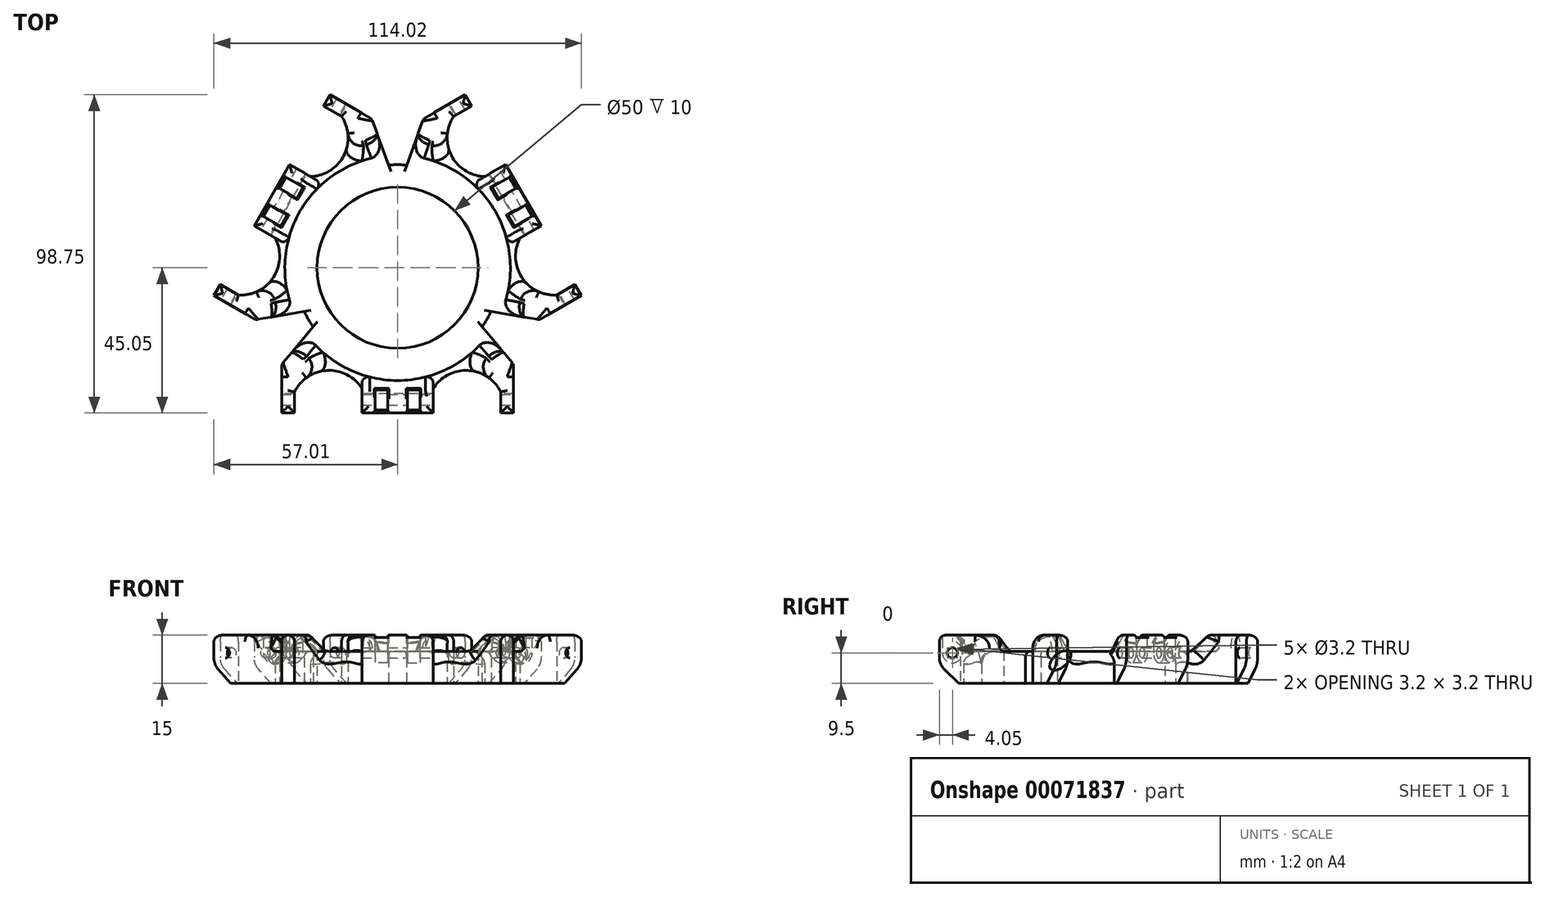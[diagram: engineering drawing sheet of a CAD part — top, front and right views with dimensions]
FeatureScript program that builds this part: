
annotation { "Feature Type Name" : "Feature", "Feature Type Description" : "" }
export const myFeature = defineFeature(function(context is Context, id is Id, definition is map)
    precondition{}
    {
        {
            assignVariable(context, id + "F0", {"name" : "JointHeight", "anyValue" : 18});
        }
        {
            var Q0;
            Q0=qCreatedBy(makeId("Top.planeOp"),FACE);
            var sketch = newSketch(context, id + "F1", { "sketchPlane" : qUnion([Q0])});
            skCircle(sketch, "E0", {"center": v(0, 0) * mm, "radius": 25 * mm});
            skCircle(sketch, "E1", {"center": v(0, 0) * mm, "radius": 32 * mm});
            skSolve(sketch);
        }
        {
            var Q0;
            Q0=qCreatedBy(makeId("Top.planeOp"),FACE);
            var sketch = newSketch(context, id + "F2", { "sketchPlane" : qUnion([Q0])});
            skLineSegment(sketch, "E2", {"start": v(-21.5, 50) * mm, "end": v(-21.5, -50) * mm, "construction": true});
            skLineSegment(sketch, "E3", {"start": v(21.5, 50) * mm, "end": v(21.5, -50) * mm, "construction": true});
            skLineSegment(sketch, "E4", {"start": v(-11, -50) * mm, "end": v(-11, -30.05) * mm, "construction": true});
            skLineSegment(sketch, "E5", {"start": v(11, -50) * mm, "end": v(11, -30.05) * mm, "construction": true});
            skLineSegment(sketch, "E6", {"start": v(-32, -50) * mm, "end": v(-32, 0) * mm, "construction": true});
            skLineSegment(sketch, "E7", {"start": v(32, -50) * mm, "end": v(32, 0) * mm, "construction": true});
            skLineSegment(sketch, "E8", {"start": v(0, -41.5) * mm, "end": v(0, -32) * mm, "construction": true});
            skLineSegment(sketch, "E9", {"start": v(-11, -30.05) * mm, "end": v(-11, -45.05) * mm});
            skLineSegment(sketch, "E10", {"start": v(-11, -45.05) * mm, "end": v(11, -45.05) * mm});
            skLineSegment(sketch, "E11", {"start": v(11, -45.05) * mm, "end": v(11, -30.05) * mm});
            skLineSegment(sketch, "E12", {"start": v(-32, -45.05) * mm, "end": v(-36, -45.05) * mm});
            skArc(sketch, "E13", {"start": v(-11, -30.05) * mm, "mid": v(0, -32) * mm, "end": v(11, -30.05) * mm});
            skLineSegment(sketch, "E14", {"start": v(-36, -45.05) * mm, "end": v(-36, -30.05) * mm});
            skLineSegment(sketch, "E15", {"start": v(-36, -30.05) * mm, "end": v(-26.2, -18.37) * mm});
            skCircle(sketch, "E16", {"center": v(-21.5, -41.5) * mm, "radius": 9.25 * mm, "construction": true});
            skLineSegment(sketch, "E17", {"start": v(-32, -45.05) * mm, "end": v(-32, -38.55) * mm});
            skArc(sketch, "E18", {"start": v(-11, -37.55) * mm, "mid": v(-21.8, -31.88) * mm, "end": v(-32, -38.55) * mm});
            skArc(sketch, "E19", {"start": v(-26.2, -18.37) * mm, "mid": v(-19.5, -25.38) * mm, "end": v(-11, -30.05) * mm});
            skLineSegment(sketch, "E20.MirrorCS", {"start": v(36, -45.05) * mm, "end": v(36, -30.05) * mm});
            skLineSegment(sketch, "E21.MirrorCS", {"start": v(32, -45.05) * mm, "end": v(36, -45.05) * mm});
            skLineSegment(sketch, "E22.MirrorCS", {"start": v(36, -30.05) * mm, "end": v(26.2, -18.37) * mm});
            skLineSegment(sketch, "E23.MirrorCS", {"start": v(32, -45.05) * mm, "end": v(32, -38.55) * mm});
            skArc(sketch, "E24.MirrorCS", {"start": v(11, -37.55) * mm, "mid": v(21.8, -31.88) * mm, "end": v(32, -38.55) * mm});
            skArc(sketch, "E25.MirrorCS", {"start": v(26.2, -18.37) * mm, "mid": v(19.5, -25.38) * mm, "end": v(11, -30.05) * mm});
            skSolve(sketch);
        }
        {
            var Q0;
            Q0=makeQuery(id+"F1.imprint","IMPRINT",FACE,{"disambiguationData":[TD([[makeQuery(id+"F1.imprint","IMPRINT",EDGE,{"derivedFrom":sQuery(id+"F1.wireOp",EDGE,"E0")}),-1.0]])]});
            extrude(context, id + "F3", {"entities" : qUnion([Q0]), "depth" : 10 * mm});
        }
        {
            var Q0;
            Q0=qSketchRegion(id+"F2",true);
            extrude(context, id + "F4", {"entities" : qUnion([Q0]), "depth" : (getVariable(context, 'JointHeight') - 3) * mm});
        }
        {
            var Q0;
            Q0=makeQuery(id+"F4.opExtrude","SWEPT_FACE",FACE,{"disambiguationData":[OSD([sQuery(id+"F2.wireOp",EDGE,"E20.MirrorCS")])]});
            var sketch = newSketch(context, id + "F5", { "sketchPlane" : qUnion([Q0])});
            skCircle(sketch, "E26", {"center": v(-41, 9.5) * mm, "radius": 1.6 * mm});
            skSolve(sketch);
        }
        {
            var Q0;
            Q0=makeQuery(id+"F5.imprint","IMPRINT",FACE,{"disambiguationData":[TD([[makeQuery(id+"F5.imprint","IMPRINT",EDGE,{"derivedFrom":sQuery(id+"F5.wireOp",EDGE,"E26")}),1.0]])]});
            var Q1;
            Q1=makeQuery(id+"F4.opExtrude","SWEPT_FACE",FACE,{"disambiguationData":[OSD([sQuery(id+"F2.wireOp",EDGE,"E14")])]});
            extrude(context, id + "F6", {"entities" : qUnion([Q0]), "operationType" : NewBodyOperationType.REMOVE, "endBound" : BoundingType.UP_TO_SURFACE, "oppositeDirection" : true, "endBoundEntityFace" : qUnion([Q1]), "depth" : 25 * mm});
        }
        {
            var Q0;
            Q0=makeQuery(id+"F4.opExtrude","SWEPT_BODY",BODY,{"disambiguationData":[OSD([sQuery(id+"F2.wireOp",EDGE,"E9"),sQuery(id+"F2.wireOp",EDGE,"E10"),sQuery(id+"F2.wireOp",EDGE,"E11"),sQuery(id+"F2.wireOp",EDGE,"E12"),sQuery(id+"F2.wireOp",EDGE,"E13"),sQuery(id+"F2.wireOp",EDGE,"E14"),sQuery(id+"F2.wireOp",EDGE,"E15"),sQuery(id+"F2.wireOp",EDGE,"E17"),sQuery(id+"F2.wireOp",EDGE,"E18"),sQuery(id+"F2.wireOp",EDGE,"E19"),sQuery(id+"F2.wireOp",EDGE,"E20.MirrorCS"),sQuery(id+"F2.wireOp",EDGE,"E21.MirrorCS"),sQuery(id+"F2.wireOp",EDGE,"E22.MirrorCS"),sQuery(id+"F2.wireOp",EDGE,"E23.MirrorCS"),sQuery(id+"F2.wireOp",EDGE,"E24.MirrorCS"),sQuery(id+"F2.wireOp",EDGE,"E25.MirrorCS")])]});
            var Q1;
            Q1=makeQuery(id+"F3.opExtrude","SWEPT_FACE",FACE,{"disambiguationData":[OSD([sQuery(id+"F1.wireOp",EDGE,"E1")])]});
            circularPattern(context, id + "F7", {"operationType" : NewBodyOperationType.ADD, "entities" : qUnion([Q0]), "axis" : qUnion([Q1]), "angle" : 120 * degree, "instanceCount" : round(3)});
        }
        {
            var Q0;
            Q0=makeQuery(id+"F4.opExtrude","CAP_EDGE",EDGE,{"disambiguationData":[OSD([sQuery(id+"F2.wireOp",EDGE,"E13"),sQuery(id+"F2.wireOp",EDGE,"E19"),sQuery(id+"F2.wireOp",EDGE,"E25.MirrorCS")])],"isStart":false});
            var Q1;
            Q1=makeQuery(id+"F7.opPattern","COPY",EDGE,{"derivedFrom":makeQuery(id+"F4.opExtrude","CAP_EDGE",EDGE,{"disambiguationData":[OSD([sQuery(id+"F2.wireOp",EDGE,"E13"),sQuery(id+"F2.wireOp",EDGE,"E19"),sQuery(id+"F2.wireOp",EDGE,"E25.MirrorCS")])],"isStart":false}),"instanceName":"1"});
            var Q2;
            Q2=makeQuery(id+"F7.opPattern","COPY",EDGE,{"derivedFrom":makeQuery(id+"F4.opExtrude","CAP_EDGE",EDGE,{"disambiguationData":[OSD([sQuery(id+"F2.wireOp",EDGE,"E13"),sQuery(id+"F2.wireOp",EDGE,"E19"),sQuery(id+"F2.wireOp",EDGE,"E25.MirrorCS")])],"isStart":false}),"instanceName":"2"});
            chamfer(context, id + "F8", {"entities" : qUnion([Q0, Q1, Q2]), "width" : 8 * mm});
        }
        {
            var Q0;
            Q0=makeQuery(id+"F8.opChamfer","BLEND_EDGE",EDGE,{"blendedFrom":[makeQuery(id+"F4.opExtrude","CAP_EDGE",EDGE,{"disambiguationData":[OSD([sQuery(id+"F2.wireOp",EDGE,"E13"),sQuery(id+"F2.wireOp",EDGE,"E19"),sQuery(id+"F2.wireOp",EDGE,"E25.MirrorCS")])],"isStart":false}),makeQuery(id+"F4.opExtrude","SWEPT_FACE",FACE,{"disambiguationData":[OSD([sQuery(id+"F2.wireOp",EDGE,"E24.MirrorCS")])]})],"blendedInto":[makeQuery(id+"F4.opExtrude","SWEPT_FACE",FACE,{"disambiguationData":[OSD([sQuery(id+"F2.wireOp",EDGE,"E24.MirrorCS")])]})]});
            var Q1;
            Q1=makeQuery(id+"F8.opChamfer","BLEND_EDGE",EDGE,{"blendedFrom":[makeQuery(id+"F4.opExtrude","CAP_EDGE",EDGE,{"disambiguationData":[OSD([sQuery(id+"F2.wireOp",EDGE,"E13"),sQuery(id+"F2.wireOp",EDGE,"E19"),sQuery(id+"F2.wireOp",EDGE,"E25.MirrorCS")])],"isStart":false}),makeQuery(id+"F4.opExtrude","SWEPT_FACE",FACE,{"disambiguationData":[OSD([sQuery(id+"F2.wireOp",EDGE,"E18")])]})],"blendedInto":[makeQuery(id+"F4.opExtrude","SWEPT_FACE",FACE,{"disambiguationData":[OSD([sQuery(id+"F2.wireOp",EDGE,"E18")])]})]});
            var Q2;
            Q2=makeQuery(id+"F8.opChamfer","BLEND_EDGE",EDGE,{"blendedFrom":[makeQuery(id+"F4.opExtrude","CAP_EDGE",EDGE,{"disambiguationData":[OSD([sQuery(id+"F2.wireOp",EDGE,"E13"),sQuery(id+"F2.wireOp",EDGE,"E19"),sQuery(id+"F2.wireOp",EDGE,"E25.MirrorCS")])],"isStart":false}),makeQuery(id+"F4.opExtrude","SWEPT_FACE",FACE,{"disambiguationData":[OSD([sQuery(id+"F2.wireOp",EDGE,"E22.MirrorCS")])]})],"blendedInto":[makeQuery(id+"F4.opExtrude","SWEPT_FACE",FACE,{"disambiguationData":[OSD([sQuery(id+"F2.wireOp",EDGE,"E22.MirrorCS")])]})]});
            var Q3;
            Q3=makeQuery(id+"F8.opChamfer","BLEND_EDGE",EDGE,{"blendedFrom":[makeQuery(id+"F4.opExtrude","CAP_EDGE",EDGE,{"disambiguationData":[OSD([sQuery(id+"F2.wireOp",EDGE,"E13"),sQuery(id+"F2.wireOp",EDGE,"E19"),sQuery(id+"F2.wireOp",EDGE,"E25.MirrorCS")])],"isStart":false}),makeQuery(id+"F4.opExtrude","SWEPT_FACE",FACE,{"disambiguationData":[OSD([sQuery(id+"F2.wireOp",EDGE,"E15")])]})],"blendedInto":[makeQuery(id+"F4.opExtrude","SWEPT_FACE",FACE,{"disambiguationData":[OSD([sQuery(id+"F2.wireOp",EDGE,"E15")])]})]});
            var Q4;
            Q4=makeQuery(id+"F8.opChamfer","BLEND_EDGE",EDGE,{"blendedFrom":[makeQuery(id+"F7.opPattern","COPY",EDGE,{"derivedFrom":makeQuery(id+"F4.opExtrude","CAP_EDGE",EDGE,{"disambiguationData":[OSD([sQuery(id+"F2.wireOp",EDGE,"E13"),sQuery(id+"F2.wireOp",EDGE,"E19"),sQuery(id+"F2.wireOp",EDGE,"E25.MirrorCS")])],"isStart":false}),"instanceName":"2"}),makeQuery(id+"F7.opPattern","COPY",FACE,{"derivedFrom":makeQuery(id+"F4.opExtrude","SWEPT_FACE",FACE,{"disambiguationData":[OSD([sQuery(id+"F2.wireOp",EDGE,"E18")])]}),"instanceName":"2"})],"blendedInto":[makeQuery(id+"F7.opPattern","COPY",FACE,{"derivedFrom":makeQuery(id+"F4.opExtrude","SWEPT_FACE",FACE,{"disambiguationData":[OSD([sQuery(id+"F2.wireOp",EDGE,"E18")])]}),"instanceName":"2"})]});
            var Q5;
            Q5=makeQuery(id+"F8.opChamfer","BLEND_EDGE",EDGE,{"blendedFrom":[makeQuery(id+"F7.opPattern","COPY",EDGE,{"derivedFrom":makeQuery(id+"F4.opExtrude","CAP_EDGE",EDGE,{"disambiguationData":[OSD([sQuery(id+"F2.wireOp",EDGE,"E13"),sQuery(id+"F2.wireOp",EDGE,"E19"),sQuery(id+"F2.wireOp",EDGE,"E25.MirrorCS")])],"isStart":false}),"instanceName":"1"}),makeQuery(id+"F7.opPattern","COPY",FACE,{"derivedFrom":makeQuery(id+"F4.opExtrude","SWEPT_FACE",FACE,{"disambiguationData":[OSD([sQuery(id+"F2.wireOp",EDGE,"E24.MirrorCS")])]}),"instanceName":"1"})],"blendedInto":[makeQuery(id+"F7.opPattern","COPY",FACE,{"derivedFrom":makeQuery(id+"F4.opExtrude","SWEPT_FACE",FACE,{"disambiguationData":[OSD([sQuery(id+"F2.wireOp",EDGE,"E24.MirrorCS")])]}),"instanceName":"1"})]});
            var Q6;
            Q6=makeQuery(id+"F8.opChamfer","BLEND_EDGE",EDGE,{"blendedFrom":[makeQuery(id+"F7.opPattern","COPY",EDGE,{"derivedFrom":makeQuery(id+"F4.opExtrude","CAP_EDGE",EDGE,{"disambiguationData":[OSD([sQuery(id+"F2.wireOp",EDGE,"E13"),sQuery(id+"F2.wireOp",EDGE,"E19"),sQuery(id+"F2.wireOp",EDGE,"E25.MirrorCS")])],"isStart":false}),"instanceName":"1"}),makeQuery(id+"F7.opPattern","COPY",FACE,{"derivedFrom":makeQuery(id+"F4.opExtrude","SWEPT_FACE",FACE,{"disambiguationData":[OSD([sQuery(id+"F2.wireOp",EDGE,"E18")])]}),"instanceName":"1"})],"blendedInto":[makeQuery(id+"F7.opPattern","COPY",FACE,{"derivedFrom":makeQuery(id+"F4.opExtrude","SWEPT_FACE",FACE,{"disambiguationData":[OSD([sQuery(id+"F2.wireOp",EDGE,"E18")])]}),"instanceName":"1"})]});
            var Q7;
            Q7=makeQuery(id+"F8.opChamfer","BLEND_EDGE",EDGE,{"blendedFrom":[makeQuery(id+"F7.opPattern","COPY",EDGE,{"derivedFrom":makeQuery(id+"F4.opExtrude","CAP_EDGE",EDGE,{"disambiguationData":[OSD([sQuery(id+"F2.wireOp",EDGE,"E13"),sQuery(id+"F2.wireOp",EDGE,"E19"),sQuery(id+"F2.wireOp",EDGE,"E25.MirrorCS")])],"isStart":false}),"instanceName":"2"}),makeQuery(id+"F7.opPattern","COPY",FACE,{"derivedFrom":makeQuery(id+"F4.opExtrude","SWEPT_FACE",FACE,{"disambiguationData":[OSD([sQuery(id+"F2.wireOp",EDGE,"E24.MirrorCS")])]}),"instanceName":"2"})],"blendedInto":[makeQuery(id+"F7.opPattern","COPY",FACE,{"derivedFrom":makeQuery(id+"F4.opExtrude","SWEPT_FACE",FACE,{"disambiguationData":[OSD([sQuery(id+"F2.wireOp",EDGE,"E24.MirrorCS")])]}),"instanceName":"2"})]});
            var Q8;
            Q8=makeQuery(id+"F8.opChamfer","BLEND_EDGE",EDGE,{"blendedFrom":[makeQuery(id+"F7.opPattern","COPY",EDGE,{"derivedFrom":makeQuery(id+"F4.opExtrude","CAP_EDGE",EDGE,{"disambiguationData":[OSD([sQuery(id+"F2.wireOp",EDGE,"E13"),sQuery(id+"F2.wireOp",EDGE,"E19"),sQuery(id+"F2.wireOp",EDGE,"E25.MirrorCS")])],"isStart":false}),"instanceName":"1"}),makeQuery(id+"F7.opPattern","COPY",FACE,{"derivedFrom":makeQuery(id+"F4.opExtrude","SWEPT_FACE",FACE,{"disambiguationData":[OSD([sQuery(id+"F2.wireOp",EDGE,"E22.MirrorCS")])]}),"instanceName":"1"})],"blendedInto":[makeQuery(id+"F7.opPattern","COPY",FACE,{"derivedFrom":makeQuery(id+"F4.opExtrude","SWEPT_FACE",FACE,{"disambiguationData":[OSD([sQuery(id+"F2.wireOp",EDGE,"E22.MirrorCS")])]}),"instanceName":"1"})]});
            var Q9;
            Q9=makeQuery(id+"F8.opChamfer","BLEND_EDGE",EDGE,{"blendedFrom":[makeQuery(id+"F7.opPattern","COPY",EDGE,{"derivedFrom":makeQuery(id+"F4.opExtrude","CAP_EDGE",EDGE,{"disambiguationData":[OSD([sQuery(id+"F2.wireOp",EDGE,"E13"),sQuery(id+"F2.wireOp",EDGE,"E19"),sQuery(id+"F2.wireOp",EDGE,"E25.MirrorCS")])],"isStart":false}),"instanceName":"1"}),makeQuery(id+"F7.opPattern","COPY",FACE,{"derivedFrom":makeQuery(id+"F4.opExtrude","SWEPT_FACE",FACE,{"disambiguationData":[OSD([sQuery(id+"F2.wireOp",EDGE,"E15")])]}),"instanceName":"1"})],"blendedInto":[makeQuery(id+"F7.opPattern","COPY",FACE,{"derivedFrom":makeQuery(id+"F4.opExtrude","SWEPT_FACE",FACE,{"disambiguationData":[OSD([sQuery(id+"F2.wireOp",EDGE,"E15")])]}),"instanceName":"1"})]});
            var Q10;
            Q10=makeQuery(id+"F8.opChamfer","BLEND_EDGE",EDGE,{"blendedFrom":[makeQuery(id+"F7.opPattern","COPY",EDGE,{"derivedFrom":makeQuery(id+"F4.opExtrude","CAP_EDGE",EDGE,{"disambiguationData":[OSD([sQuery(id+"F2.wireOp",EDGE,"E13"),sQuery(id+"F2.wireOp",EDGE,"E19"),sQuery(id+"F2.wireOp",EDGE,"E25.MirrorCS")])],"isStart":false}),"instanceName":"2"}),makeQuery(id+"F7.opPattern","COPY",FACE,{"derivedFrom":makeQuery(id+"F4.opExtrude","SWEPT_FACE",FACE,{"disambiguationData":[OSD([sQuery(id+"F2.wireOp",EDGE,"E22.MirrorCS")])]}),"instanceName":"2"})],"blendedInto":[makeQuery(id+"F7.opPattern","COPY",FACE,{"derivedFrom":makeQuery(id+"F4.opExtrude","SWEPT_FACE",FACE,{"disambiguationData":[OSD([sQuery(id+"F2.wireOp",EDGE,"E22.MirrorCS")])]}),"instanceName":"2"})]});
            var Q11;
            Q11=makeQuery(id+"F7.opPattern","COPY",EDGE,{"derivedFrom":makeQuery(id+"F4.opExtrude","CAP_EDGE",EDGE,{"disambiguationData":[OSD([sQuery(id+"F2.wireOp",EDGE,"E15")])],"isStart":false}),"instanceName":"2"});
            var Q12;
            Q12=makeQuery(id+"F4.opExtrude","CAP_EDGE",EDGE,{"disambiguationData":[OSD([sQuery(id+"F2.wireOp",EDGE,"E22.MirrorCS")])],"isStart":false});
            var Q13;
            Q13=makeQuery(id+"F8.opChamfer","BLEND_EDGE",EDGE,{"blendedFrom":[makeQuery(id+"F7.opPattern","COPY",EDGE,{"derivedFrom":makeQuery(id+"F4.opExtrude","CAP_EDGE",EDGE,{"disambiguationData":[OSD([sQuery(id+"F2.wireOp",EDGE,"E13"),sQuery(id+"F2.wireOp",EDGE,"E19"),sQuery(id+"F2.wireOp",EDGE,"E25.MirrorCS")])],"isStart":false}),"instanceName":"2"}),makeQuery(id+"F7.opPattern","COPY",FACE,{"derivedFrom":makeQuery(id+"F4.opExtrude","SWEPT_FACE",FACE,{"disambiguationData":[OSD([sQuery(id+"F2.wireOp",EDGE,"E15")])]}),"instanceName":"2"})],"blendedInto":[makeQuery(id+"F7.opPattern","COPY",FACE,{"derivedFrom":makeQuery(id+"F4.opExtrude","SWEPT_FACE",FACE,{"disambiguationData":[OSD([sQuery(id+"F2.wireOp",EDGE,"E15")])]}),"instanceName":"2"})]});
            var Q14;
            {var subQ0=sQuery(id+"F1.wireOp",EDGE,"E1");Q14=makeQuery(id+"F8.opChamfer","TWEAK_EDGE",EDGE,{"derivedFrom":[makeQuery(id+"F7.boolean.opBoolean","TWEAK_VERTEX",VERTEX,{"derivedFrom":[makeQuery(id+"F3.opExtrude","CAP_FACE",FACE,{"disambiguationData":[OSD([sQuery(id+"F1.wireOp",EDGE,"E0"),subQ0])],"isStart":false}),makeQuery(id+"F3.opExtrude","SWEPT_FACE",FACE,{"disambiguationData":[OSD([subQ0])]}),makeQuery(id+"F7.opPattern","COPY",FACE,{"derivedFrom":makeQuery(id+"F4.opExtrude","SWEPT_FACE",FACE,{"disambiguationData":[OSD([sQuery(id+"F2.wireOp",EDGE,"E13"),sQuery(id+"F2.wireOp",EDGE,"E19"),sQuery(id+"F2.wireOp",EDGE,"E25.MirrorCS")])]}),"instanceName":"2"}),makeQuery(id+"F7.opPattern","COPY",FACE,{"derivedFrom":makeQuery(id+"F4.opExtrude","SWEPT_FACE",FACE,{"disambiguationData":[OSD([sQuery(id+"F2.wireOp",EDGE,"E22.MirrorCS")])]}),"instanceName":"2"})]})]});}
            var Q15;
            {var subQ0=sQuery(id+"F1.wireOp",EDGE,"E1");Q15=makeQuery(id+"F8.opChamfer","TWEAK_EDGE",EDGE,{"derivedFrom":[makeQuery(id+"F7.boolean.opBoolean","TWEAK_VERTEX",VERTEX,{"derivedFrom":[makeQuery(id+"F3.opExtrude","CAP_FACE",FACE,{"disambiguationData":[OSD([sQuery(id+"F1.wireOp",EDGE,"E0"),subQ0])],"isStart":false}),makeQuery(id+"F3.opExtrude","SWEPT_FACE",FACE,{"disambiguationData":[OSD([subQ0])]}),makeQuery(id+"F7.opPattern","COPY",FACE,{"derivedFrom":makeQuery(id+"F4.opExtrude","SWEPT_FACE",FACE,{"disambiguationData":[OSD([sQuery(id+"F2.wireOp",EDGE,"E13"),sQuery(id+"F2.wireOp",EDGE,"E19"),sQuery(id+"F2.wireOp",EDGE,"E25.MirrorCS")])]}),"instanceName":"1"}),makeQuery(id+"F7.opPattern","COPY",FACE,{"derivedFrom":makeQuery(id+"F4.opExtrude","SWEPT_FACE",FACE,{"disambiguationData":[OSD([sQuery(id+"F2.wireOp",EDGE,"E15")])]}),"instanceName":"1"})]})]});}
            var Q16;
            {var subQ0=sQuery(id+"F1.wireOp",EDGE,"E1");Q16=makeQuery(id+"F8.opChamfer","TWEAK_EDGE",EDGE,{"derivedFrom":[makeQuery(id+"F7.boolean.opBoolean","TWEAK_VERTEX",VERTEX,{"derivedFrom":[makeQuery(id+"F3.opExtrude","CAP_FACE",FACE,{"disambiguationData":[OSD([sQuery(id+"F1.wireOp",EDGE,"E0"),subQ0])],"isStart":false}),makeQuery(id+"F3.opExtrude","SWEPT_FACE",FACE,{"disambiguationData":[OSD([subQ0])]}),makeQuery(id+"F7.opPattern","COPY",FACE,{"derivedFrom":makeQuery(id+"F4.opExtrude","SWEPT_FACE",FACE,{"disambiguationData":[OSD([sQuery(id+"F2.wireOp",EDGE,"E13"),sQuery(id+"F2.wireOp",EDGE,"E19"),sQuery(id+"F2.wireOp",EDGE,"E25.MirrorCS")])]}),"instanceName":"1"}),makeQuery(id+"F7.opPattern","COPY",FACE,{"derivedFrom":makeQuery(id+"F4.opExtrude","SWEPT_FACE",FACE,{"disambiguationData":[OSD([sQuery(id+"F2.wireOp",EDGE,"E22.MirrorCS")])]}),"instanceName":"1"})]})]});}
            var Q17;
            {var subQ0=sQuery(id+"F1.wireOp",EDGE,"E1");Q17=makeQuery(id+"F8.opChamfer","TWEAK_EDGE",EDGE,{"derivedFrom":[makeQuery(id+"F7.boolean.opBoolean","TWEAK_VERTEX",VERTEX,{"derivedFrom":[makeQuery(id+"F3.opExtrude","CAP_FACE",FACE,{"disambiguationData":[OSD([sQuery(id+"F1.wireOp",EDGE,"E0"),subQ0])],"isStart":false}),makeQuery(id+"F3.opExtrude","SWEPT_FACE",FACE,{"disambiguationData":[OSD([subQ0])]}),makeQuery(id+"F4.opExtrude","SWEPT_FACE",FACE,{"disambiguationData":[OSD([sQuery(id+"F2.wireOp",EDGE,"E13"),sQuery(id+"F2.wireOp",EDGE,"E19"),sQuery(id+"F2.wireOp",EDGE,"E25.MirrorCS")])]}),makeQuery(id+"F4.opExtrude","SWEPT_FACE",FACE,{"disambiguationData":[OSD([sQuery(id+"F2.wireOp",EDGE,"E15")])]})]})]});}
            var Q18;
            Q18=makeQuery(id+"F4.opExtrude","CAP_EDGE",EDGE,{"disambiguationData":[OSD([sQuery(id+"F2.wireOp",EDGE,"E15")])],"isStart":false});
            var Q19;
            Q19=makeQuery(id+"F7.opPattern","COPY",EDGE,{"derivedFrom":makeQuery(id+"F4.opExtrude","CAP_EDGE",EDGE,{"disambiguationData":[OSD([sQuery(id+"F2.wireOp",EDGE,"E22.MirrorCS")])],"isStart":false}),"instanceName":"1"});
            var Q20;
            Q20=makeQuery(id+"F7.opPattern","COPY",EDGE,{"derivedFrom":makeQuery(id+"F4.opExtrude","CAP_EDGE",EDGE,{"disambiguationData":[OSD([sQuery(id+"F2.wireOp",EDGE,"E22.MirrorCS")])],"isStart":false}),"instanceName":"2"});
            var Q21;
            Q21=makeQuery(id+"F7.opPattern","COPY",EDGE,{"derivedFrom":makeQuery(id+"F4.opExtrude","CAP_EDGE",EDGE,{"disambiguationData":[OSD([sQuery(id+"F2.wireOp",EDGE,"E15")])],"isStart":false}),"instanceName":"1"});
            var Q22;
            {var subQ0=sQuery(id+"F1.wireOp",EDGE,"E1");Q22=makeQuery(id+"F8.opChamfer","TWEAK_EDGE",EDGE,{"derivedFrom":[makeQuery(id+"F7.boolean.opBoolean","TWEAK_VERTEX",VERTEX,{"derivedFrom":[makeQuery(id+"F3.opExtrude","CAP_FACE",FACE,{"disambiguationData":[OSD([sQuery(id+"F1.wireOp",EDGE,"E0"),subQ0])],"isStart":false}),makeQuery(id+"F3.opExtrude","SWEPT_FACE",FACE,{"disambiguationData":[OSD([subQ0])]}),makeQuery(id+"F7.opPattern","COPY",FACE,{"derivedFrom":makeQuery(id+"F4.opExtrude","SWEPT_FACE",FACE,{"disambiguationData":[OSD([sQuery(id+"F2.wireOp",EDGE,"E13"),sQuery(id+"F2.wireOp",EDGE,"E19"),sQuery(id+"F2.wireOp",EDGE,"E25.MirrorCS")])]}),"instanceName":"2"}),makeQuery(id+"F7.opPattern","COPY",FACE,{"derivedFrom":makeQuery(id+"F4.opExtrude","SWEPT_FACE",FACE,{"disambiguationData":[OSD([sQuery(id+"F2.wireOp",EDGE,"E15")])]}),"instanceName":"2"})]})]});}
            var Q23;
            {var subQ0=sQuery(id+"F1.wireOp",EDGE,"E1");Q23=makeQuery(id+"F8.opChamfer","TWEAK_EDGE",EDGE,{"derivedFrom":[makeQuery(id+"F7.boolean.opBoolean","TWEAK_VERTEX",VERTEX,{"derivedFrom":[makeQuery(id+"F3.opExtrude","CAP_FACE",FACE,{"disambiguationData":[OSD([sQuery(id+"F1.wireOp",EDGE,"E0"),subQ0])],"isStart":false}),makeQuery(id+"F3.opExtrude","SWEPT_FACE",FACE,{"disambiguationData":[OSD([subQ0])]}),makeQuery(id+"F4.opExtrude","SWEPT_FACE",FACE,{"disambiguationData":[OSD([sQuery(id+"F2.wireOp",EDGE,"E13"),sQuery(id+"F2.wireOp",EDGE,"E19"),sQuery(id+"F2.wireOp",EDGE,"E25.MirrorCS")])]}),makeQuery(id+"F4.opExtrude","SWEPT_FACE",FACE,{"disambiguationData":[OSD([sQuery(id+"F2.wireOp",EDGE,"E22.MirrorCS")])]})]})]});}
            fillet(context, id + "F9", {"entities" : qUnion([Q0, Q1, Q2, Q3, Q4, Q5, Q6, Q7, Q8, Q9, Q10, Q11, Q12, Q13, Q14, Q15, Q16, Q17, Q18, Q19, Q20, Q21, Q22, Q23]), "radius" : 4 * mm, "tangentPropagation" : true, "allowEdgeOverflow" : false});
        }
        {
            var Q0;
            Q0=makeQuery(id+"F8.opChamfer","BLEND_EDGE",EDGE,{"blendedFrom":[makeQuery(id+"F7.opPattern","COPY",EDGE,{"derivedFrom":makeQuery(id+"F4.opExtrude","CAP_EDGE",EDGE,{"disambiguationData":[OSD([sQuery(id+"F2.wireOp",EDGE,"E13"),sQuery(id+"F2.wireOp",EDGE,"E19"),sQuery(id+"F2.wireOp",EDGE,"E25.MirrorCS")])],"isStart":false}),"instanceName":"1"}),makeQuery(id+"F7.opPattern","COPY",FACE,{"derivedFrom":makeQuery(id+"F4.opExtrude","SWEPT_FACE",FACE,{"disambiguationData":[OSD([sQuery(id+"F2.wireOp",EDGE,"E11")])]}),"instanceName":"1"})],"blendedInto":[makeQuery(id+"F7.opPattern","COPY",FACE,{"derivedFrom":makeQuery(id+"F4.opExtrude","SWEPT_FACE",FACE,{"disambiguationData":[OSD([sQuery(id+"F2.wireOp",EDGE,"E11")])]}),"instanceName":"1"})]});
            var Q1;
            Q1=makeQuery(id+"F8.opChamfer","BLEND_EDGE",EDGE,{"blendedFrom":[makeQuery(id+"F7.opPattern","COPY",EDGE,{"derivedFrom":makeQuery(id+"F4.opExtrude","CAP_EDGE",EDGE,{"disambiguationData":[OSD([sQuery(id+"F2.wireOp",EDGE,"E13"),sQuery(id+"F2.wireOp",EDGE,"E19"),sQuery(id+"F2.wireOp",EDGE,"E25.MirrorCS")])],"isStart":false}),"instanceName":"1"}),makeQuery(id+"F7.opPattern","COPY",FACE,{"derivedFrom":makeQuery(id+"F4.opExtrude","SWEPT_FACE",FACE,{"disambiguationData":[OSD([sQuery(id+"F2.wireOp",EDGE,"E9")])]}),"instanceName":"1"})],"blendedInto":[makeQuery(id+"F7.opPattern","COPY",FACE,{"derivedFrom":makeQuery(id+"F4.opExtrude","SWEPT_FACE",FACE,{"disambiguationData":[OSD([sQuery(id+"F2.wireOp",EDGE,"E9")])]}),"instanceName":"1"})]});
            var Q2;
            Q2=makeQuery(id+"F8.opChamfer","BLEND_EDGE",EDGE,{"blendedFrom":[makeQuery(id+"F7.opPattern","COPY",EDGE,{"derivedFrom":makeQuery(id+"F4.opExtrude","CAP_EDGE",EDGE,{"disambiguationData":[OSD([sQuery(id+"F2.wireOp",EDGE,"E13"),sQuery(id+"F2.wireOp",EDGE,"E19"),sQuery(id+"F2.wireOp",EDGE,"E25.MirrorCS")])],"isStart":false}),"instanceName":"2"}),makeQuery(id+"F7.opPattern","COPY",FACE,{"derivedFrom":makeQuery(id+"F4.opExtrude","SWEPT_FACE",FACE,{"disambiguationData":[OSD([sQuery(id+"F2.wireOp",EDGE,"E11")])]}),"instanceName":"2"})],"blendedInto":[makeQuery(id+"F7.opPattern","COPY",FACE,{"derivedFrom":makeQuery(id+"F4.opExtrude","SWEPT_FACE",FACE,{"disambiguationData":[OSD([sQuery(id+"F2.wireOp",EDGE,"E11")])]}),"instanceName":"2"})]});
            var Q3;
            Q3=makeQuery(id+"F8.opChamfer","BLEND_EDGE",EDGE,{"blendedFrom":[makeQuery(id+"F7.opPattern","COPY",EDGE,{"derivedFrom":makeQuery(id+"F4.opExtrude","CAP_EDGE",EDGE,{"disambiguationData":[OSD([sQuery(id+"F2.wireOp",EDGE,"E13"),sQuery(id+"F2.wireOp",EDGE,"E19"),sQuery(id+"F2.wireOp",EDGE,"E25.MirrorCS")])],"isStart":false}),"instanceName":"2"}),makeQuery(id+"F7.opPattern","COPY",FACE,{"derivedFrom":makeQuery(id+"F4.opExtrude","SWEPT_FACE",FACE,{"disambiguationData":[OSD([sQuery(id+"F2.wireOp",EDGE,"E9")])]}),"instanceName":"2"})],"blendedInto":[makeQuery(id+"F7.opPattern","COPY",FACE,{"derivedFrom":makeQuery(id+"F4.opExtrude","SWEPT_FACE",FACE,{"disambiguationData":[OSD([sQuery(id+"F2.wireOp",EDGE,"E9")])]}),"instanceName":"2"})]});
            var Q4;
            Q4=makeQuery(id+"F8.opChamfer","BLEND_EDGE",EDGE,{"blendedFrom":[makeQuery(id+"F4.opExtrude","CAP_EDGE",EDGE,{"disambiguationData":[OSD([sQuery(id+"F2.wireOp",EDGE,"E13"),sQuery(id+"F2.wireOp",EDGE,"E19"),sQuery(id+"F2.wireOp",EDGE,"E25.MirrorCS")])],"isStart":false}),makeQuery(id+"F4.opExtrude","SWEPT_FACE",FACE,{"disambiguationData":[OSD([sQuery(id+"F2.wireOp",EDGE,"E11")])]})],"blendedInto":[makeQuery(id+"F4.opExtrude","SWEPT_FACE",FACE,{"disambiguationData":[OSD([sQuery(id+"F2.wireOp",EDGE,"E11")])]})]});
            var Q5;
            Q5=makeQuery(id+"F8.opChamfer","BLEND_EDGE",EDGE,{"blendedFrom":[makeQuery(id+"F4.opExtrude","CAP_EDGE",EDGE,{"disambiguationData":[OSD([sQuery(id+"F2.wireOp",EDGE,"E13"),sQuery(id+"F2.wireOp",EDGE,"E19"),sQuery(id+"F2.wireOp",EDGE,"E25.MirrorCS")])],"isStart":false}),makeQuery(id+"F4.opExtrude","SWEPT_FACE",FACE,{"disambiguationData":[OSD([sQuery(id+"F2.wireOp",EDGE,"E9")])]})],"blendedInto":[makeQuery(id+"F4.opExtrude","SWEPT_FACE",FACE,{"disambiguationData":[OSD([sQuery(id+"F2.wireOp",EDGE,"E9")])]})]});
            var Q6;
            Q6=makeQuery(id+"F8.opChamfer","SPLIT",FACE,{"disambiguationData":[OD(0.0)],"derivedFrom":makeQuery(id+"F4.opExtrude","CAP_FACE",FACE,{"disambiguationData":[OSD([sQuery(id+"F2.wireOp",EDGE,"E9"),sQuery(id+"F2.wireOp",EDGE,"E10"),sQuery(id+"F2.wireOp",EDGE,"E11"),sQuery(id+"F2.wireOp",EDGE,"E12"),sQuery(id+"F2.wireOp",EDGE,"E13"),sQuery(id+"F2.wireOp",EDGE,"E14"),sQuery(id+"F2.wireOp",EDGE,"E15"),sQuery(id+"F2.wireOp",EDGE,"E17"),sQuery(id+"F2.wireOp",EDGE,"E18"),sQuery(id+"F2.wireOp",EDGE,"E19"),sQuery(id+"F2.wireOp",EDGE,"E20.MirrorCS"),sQuery(id+"F2.wireOp",EDGE,"E21.MirrorCS"),sQuery(id+"F2.wireOp",EDGE,"E22.MirrorCS"),sQuery(id+"F2.wireOp",EDGE,"E23.MirrorCS"),sQuery(id+"F2.wireOp",EDGE,"E24.MirrorCS"),sQuery(id+"F2.wireOp",EDGE,"E25.MirrorCS")])],"isStart":false})});
            var Q7;
            Q7=makeQuery(id+"F8.opChamfer","SPLIT",FACE,{"disambiguationData":[OD(1.0)],"derivedFrom":makeQuery(id+"F4.opExtrude","CAP_FACE",FACE,{"disambiguationData":[OSD([sQuery(id+"F2.wireOp",EDGE,"E9"),sQuery(id+"F2.wireOp",EDGE,"E10"),sQuery(id+"F2.wireOp",EDGE,"E11"),sQuery(id+"F2.wireOp",EDGE,"E12"),sQuery(id+"F2.wireOp",EDGE,"E13"),sQuery(id+"F2.wireOp",EDGE,"E14"),sQuery(id+"F2.wireOp",EDGE,"E15"),sQuery(id+"F2.wireOp",EDGE,"E17"),sQuery(id+"F2.wireOp",EDGE,"E18"),sQuery(id+"F2.wireOp",EDGE,"E19"),sQuery(id+"F2.wireOp",EDGE,"E20.MirrorCS"),sQuery(id+"F2.wireOp",EDGE,"E21.MirrorCS"),sQuery(id+"F2.wireOp",EDGE,"E22.MirrorCS"),sQuery(id+"F2.wireOp",EDGE,"E23.MirrorCS"),sQuery(id+"F2.wireOp",EDGE,"E24.MirrorCS"),sQuery(id+"F2.wireOp",EDGE,"E25.MirrorCS")])],"isStart":false})});
            var Q8;
            Q8=makeQuery(id+"F8.opChamfer","SPLIT",FACE,{"disambiguationData":[OD(2.0)],"derivedFrom":makeQuery(id+"F7.opPattern","COPY",FACE,{"derivedFrom":makeQuery(id+"F4.opExtrude","CAP_FACE",FACE,{"disambiguationData":[OSD([sQuery(id+"F2.wireOp",EDGE,"E9"),sQuery(id+"F2.wireOp",EDGE,"E10"),sQuery(id+"F2.wireOp",EDGE,"E11"),sQuery(id+"F2.wireOp",EDGE,"E12"),sQuery(id+"F2.wireOp",EDGE,"E13"),sQuery(id+"F2.wireOp",EDGE,"E14"),sQuery(id+"F2.wireOp",EDGE,"E15"),sQuery(id+"F2.wireOp",EDGE,"E17"),sQuery(id+"F2.wireOp",EDGE,"E18"),sQuery(id+"F2.wireOp",EDGE,"E19"),sQuery(id+"F2.wireOp",EDGE,"E20.MirrorCS"),sQuery(id+"F2.wireOp",EDGE,"E21.MirrorCS"),sQuery(id+"F2.wireOp",EDGE,"E22.MirrorCS"),sQuery(id+"F2.wireOp",EDGE,"E23.MirrorCS"),sQuery(id+"F2.wireOp",EDGE,"E24.MirrorCS"),sQuery(id+"F2.wireOp",EDGE,"E25.MirrorCS")])],"isStart":false}),"instanceName":"1"})});
            var Q9;
            Q9=makeQuery(id+"F8.opChamfer","SPLIT",FACE,{"disambiguationData":[OD(1.0)],"derivedFrom":makeQuery(id+"F7.opPattern","COPY",FACE,{"derivedFrom":makeQuery(id+"F4.opExtrude","CAP_FACE",FACE,{"disambiguationData":[OSD([sQuery(id+"F2.wireOp",EDGE,"E9"),sQuery(id+"F2.wireOp",EDGE,"E10"),sQuery(id+"F2.wireOp",EDGE,"E11"),sQuery(id+"F2.wireOp",EDGE,"E12"),sQuery(id+"F2.wireOp",EDGE,"E13"),sQuery(id+"F2.wireOp",EDGE,"E14"),sQuery(id+"F2.wireOp",EDGE,"E15"),sQuery(id+"F2.wireOp",EDGE,"E17"),sQuery(id+"F2.wireOp",EDGE,"E18"),sQuery(id+"F2.wireOp",EDGE,"E19"),sQuery(id+"F2.wireOp",EDGE,"E20.MirrorCS"),sQuery(id+"F2.wireOp",EDGE,"E21.MirrorCS"),sQuery(id+"F2.wireOp",EDGE,"E22.MirrorCS"),sQuery(id+"F2.wireOp",EDGE,"E23.MirrorCS"),sQuery(id+"F2.wireOp",EDGE,"E24.MirrorCS"),sQuery(id+"F2.wireOp",EDGE,"E25.MirrorCS")])],"isStart":false}),"instanceName":"1"})});
            var Q10;
            Q10=makeQuery(id+"F8.opChamfer","SPLIT",FACE,{"disambiguationData":[OD(0.0)],"derivedFrom":makeQuery(id+"F7.opPattern","COPY",FACE,{"derivedFrom":makeQuery(id+"F4.opExtrude","CAP_FACE",FACE,{"disambiguationData":[OSD([sQuery(id+"F2.wireOp",EDGE,"E9"),sQuery(id+"F2.wireOp",EDGE,"E10"),sQuery(id+"F2.wireOp",EDGE,"E11"),sQuery(id+"F2.wireOp",EDGE,"E12"),sQuery(id+"F2.wireOp",EDGE,"E13"),sQuery(id+"F2.wireOp",EDGE,"E14"),sQuery(id+"F2.wireOp",EDGE,"E15"),sQuery(id+"F2.wireOp",EDGE,"E17"),sQuery(id+"F2.wireOp",EDGE,"E18"),sQuery(id+"F2.wireOp",EDGE,"E19"),sQuery(id+"F2.wireOp",EDGE,"E20.MirrorCS"),sQuery(id+"F2.wireOp",EDGE,"E21.MirrorCS"),sQuery(id+"F2.wireOp",EDGE,"E22.MirrorCS"),sQuery(id+"F2.wireOp",EDGE,"E23.MirrorCS"),sQuery(id+"F2.wireOp",EDGE,"E24.MirrorCS"),sQuery(id+"F2.wireOp",EDGE,"E25.MirrorCS")])],"isStart":false}),"instanceName":"1"})});
            var Q11;
            Q11=makeQuery(id+"F8.opChamfer","SPLIT",FACE,{"disambiguationData":[OD(2.0)],"derivedFrom":makeQuery(id+"F7.opPattern","COPY",FACE,{"derivedFrom":makeQuery(id+"F4.opExtrude","CAP_FACE",FACE,{"disambiguationData":[OSD([sQuery(id+"F2.wireOp",EDGE,"E9"),sQuery(id+"F2.wireOp",EDGE,"E10"),sQuery(id+"F2.wireOp",EDGE,"E11"),sQuery(id+"F2.wireOp",EDGE,"E12"),sQuery(id+"F2.wireOp",EDGE,"E13"),sQuery(id+"F2.wireOp",EDGE,"E14"),sQuery(id+"F2.wireOp",EDGE,"E15"),sQuery(id+"F2.wireOp",EDGE,"E17"),sQuery(id+"F2.wireOp",EDGE,"E18"),sQuery(id+"F2.wireOp",EDGE,"E19"),sQuery(id+"F2.wireOp",EDGE,"E20.MirrorCS"),sQuery(id+"F2.wireOp",EDGE,"E21.MirrorCS"),sQuery(id+"F2.wireOp",EDGE,"E22.MirrorCS"),sQuery(id+"F2.wireOp",EDGE,"E23.MirrorCS"),sQuery(id+"F2.wireOp",EDGE,"E24.MirrorCS"),sQuery(id+"F2.wireOp",EDGE,"E25.MirrorCS")])],"isStart":false}),"instanceName":"2"})});
            var Q12;
            Q12=makeQuery(id+"F8.opChamfer","SPLIT",FACE,{"disambiguationData":[OD(0.0)],"derivedFrom":makeQuery(id+"F7.opPattern","COPY",FACE,{"derivedFrom":makeQuery(id+"F4.opExtrude","CAP_FACE",FACE,{"disambiguationData":[OSD([sQuery(id+"F2.wireOp",EDGE,"E9"),sQuery(id+"F2.wireOp",EDGE,"E10"),sQuery(id+"F2.wireOp",EDGE,"E11"),sQuery(id+"F2.wireOp",EDGE,"E12"),sQuery(id+"F2.wireOp",EDGE,"E13"),sQuery(id+"F2.wireOp",EDGE,"E14"),sQuery(id+"F2.wireOp",EDGE,"E15"),sQuery(id+"F2.wireOp",EDGE,"E17"),sQuery(id+"F2.wireOp",EDGE,"E18"),sQuery(id+"F2.wireOp",EDGE,"E19"),sQuery(id+"F2.wireOp",EDGE,"E20.MirrorCS"),sQuery(id+"F2.wireOp",EDGE,"E21.MirrorCS"),sQuery(id+"F2.wireOp",EDGE,"E22.MirrorCS"),sQuery(id+"F2.wireOp",EDGE,"E23.MirrorCS"),sQuery(id+"F2.wireOp",EDGE,"E24.MirrorCS"),sQuery(id+"F2.wireOp",EDGE,"E25.MirrorCS")])],"isStart":false}),"instanceName":"2"})});
            var Q13;
            Q13=makeQuery(id+"F8.opChamfer","SPLIT",FACE,{"disambiguationData":[OD(1.0)],"derivedFrom":makeQuery(id+"F7.opPattern","COPY",FACE,{"derivedFrom":makeQuery(id+"F4.opExtrude","CAP_FACE",FACE,{"disambiguationData":[OSD([sQuery(id+"F2.wireOp",EDGE,"E9"),sQuery(id+"F2.wireOp",EDGE,"E10"),sQuery(id+"F2.wireOp",EDGE,"E11"),sQuery(id+"F2.wireOp",EDGE,"E12"),sQuery(id+"F2.wireOp",EDGE,"E13"),sQuery(id+"F2.wireOp",EDGE,"E14"),sQuery(id+"F2.wireOp",EDGE,"E15"),sQuery(id+"F2.wireOp",EDGE,"E17"),sQuery(id+"F2.wireOp",EDGE,"E18"),sQuery(id+"F2.wireOp",EDGE,"E19"),sQuery(id+"F2.wireOp",EDGE,"E20.MirrorCS"),sQuery(id+"F2.wireOp",EDGE,"E21.MirrorCS"),sQuery(id+"F2.wireOp",EDGE,"E22.MirrorCS"),sQuery(id+"F2.wireOp",EDGE,"E23.MirrorCS"),sQuery(id+"F2.wireOp",EDGE,"E24.MirrorCS"),sQuery(id+"F2.wireOp",EDGE,"E25.MirrorCS")])],"isStart":false}),"instanceName":"2"})});
            var Q14;
            Q14=makeQuery(id+"F8.opChamfer","SPLIT",FACE,{"disambiguationData":[OD(2.0)],"derivedFrom":makeQuery(id+"F4.opExtrude","CAP_FACE",FACE,{"disambiguationData":[OSD([sQuery(id+"F2.wireOp",EDGE,"E9"),sQuery(id+"F2.wireOp",EDGE,"E10"),sQuery(id+"F2.wireOp",EDGE,"E11"),sQuery(id+"F2.wireOp",EDGE,"E12"),sQuery(id+"F2.wireOp",EDGE,"E13"),sQuery(id+"F2.wireOp",EDGE,"E14"),sQuery(id+"F2.wireOp",EDGE,"E15"),sQuery(id+"F2.wireOp",EDGE,"E17"),sQuery(id+"F2.wireOp",EDGE,"E18"),sQuery(id+"F2.wireOp",EDGE,"E19"),sQuery(id+"F2.wireOp",EDGE,"E20.MirrorCS"),sQuery(id+"F2.wireOp",EDGE,"E21.MirrorCS"),sQuery(id+"F2.wireOp",EDGE,"E22.MirrorCS"),sQuery(id+"F2.wireOp",EDGE,"E23.MirrorCS"),sQuery(id+"F2.wireOp",EDGE,"E24.MirrorCS"),sQuery(id+"F2.wireOp",EDGE,"E25.MirrorCS")])],"isStart":false})});
            fillet(context, id + "F10", {"entities" : qUnion([Q0, Q1, Q2, Q3, Q4, Q5, Q6, Q7, Q8, Q9, Q10, Q11, Q12, Q13, Q14]), "radius" : 2 * mm, "tangentPropagation" : true, "allowEdgeOverflow" : false});
        }
        {
            var Q0;
            {var subQ0=sQuery(id+"F1.wireOp",EDGE,"E1");Q0=makeQuery(id+"F8.opChamfer","TWEAK_EDGE",EDGE,{"derivedFrom":[makeQuery(id+"F7.boolean.opBoolean","TWEAK_VERTEX",VERTEX,{"derivedFrom":[makeQuery(id+"F3.opExtrude","CAP_FACE",FACE,{"disambiguationData":[OSD([sQuery(id+"F1.wireOp",EDGE,"E0"),subQ0])],"isStart":false}),makeQuery(id+"F3.opExtrude","SWEPT_FACE",FACE,{"disambiguationData":[OSD([subQ0])]}),makeQuery(id+"F4.opExtrude","SWEPT_FACE",FACE,{"disambiguationData":[OSD([sQuery(id+"F2.wireOp",EDGE,"E13"),sQuery(id+"F2.wireOp",EDGE,"E19"),sQuery(id+"F2.wireOp",EDGE,"E25.MirrorCS")])]}),makeQuery(id+"F4.opExtrude","SWEPT_FACE",FACE,{"disambiguationData":[OSD([sQuery(id+"F2.wireOp",EDGE,"E15")])]})]})]});}
            var Q1;
            {var subQ0=makeQuery(id+"F4.opExtrude","SWEPT_FACE",FACE,{"disambiguationData":[OSD([sQuery(id+"F2.wireOp",EDGE,"E13"),sQuery(id+"F2.wireOp",EDGE,"E19"),sQuery(id+"F2.wireOp",EDGE,"E25.MirrorCS")])]});var subQ1=sQuery(id+"F1.wireOp",EDGE,"E1");Q1=makeQuery(id+"F7.boolean.opBoolean","SPLIT",EDGE,{"disambiguationData":[TD([makeQuery(id+"F3.opExtrude","CAP_FACE",FACE,{"disambiguationData":[OSD([sQuery(id+"F1.wireOp",EDGE,"E0"),subQ1])],"isStart":false}),makeQuery(id+"F3.opExtrude","SWEPT_FACE",FACE,{"disambiguationData":[OSD([subQ1])]}),subQ0,makeQuery(id+"F4.opExtrude","SWEPT_FACE",FACE,{"disambiguationData":[OSD([sQuery(id+"F2.wireOp",EDGE,"E15")])]}),makeQuery(id+"F7.opPattern","COPY",FACE,{"derivedFrom":subQ0,"instanceName":"1"}),makeQuery(id+"F7.opPattern","COPY",FACE,{"derivedFrom":makeQuery(id+"F4.opExtrude","SWEPT_FACE",FACE,{"disambiguationData":[OSD([sQuery(id+"F2.wireOp",EDGE,"E22.MirrorCS")])]}),"instanceName":"1"})])],"derivedFrom":makeQuery(id+"F3.opExtrude","CAP_EDGE",EDGE,{"disambiguationData":[OSD([subQ1])],"isStart":false})});}
            var Q2;
            {var subQ0=sQuery(id+"F1.wireOp",EDGE,"E1");Q2=makeQuery(id+"F8.opChamfer","TWEAK_EDGE",EDGE,{"derivedFrom":[makeQuery(id+"F7.boolean.opBoolean","TWEAK_VERTEX",VERTEX,{"derivedFrom":[makeQuery(id+"F3.opExtrude","CAP_FACE",FACE,{"disambiguationData":[OSD([sQuery(id+"F1.wireOp",EDGE,"E0"),subQ0])],"isStart":false}),makeQuery(id+"F3.opExtrude","SWEPT_FACE",FACE,{"disambiguationData":[OSD([subQ0])]}),makeQuery(id+"F7.opPattern","COPY",FACE,{"derivedFrom":makeQuery(id+"F4.opExtrude","SWEPT_FACE",FACE,{"disambiguationData":[OSD([sQuery(id+"F2.wireOp",EDGE,"E13"),sQuery(id+"F2.wireOp",EDGE,"E19"),sQuery(id+"F2.wireOp",EDGE,"E25.MirrorCS")])]}),"instanceName":"1"}),makeQuery(id+"F7.opPattern","COPY",FACE,{"derivedFrom":makeQuery(id+"F4.opExtrude","SWEPT_FACE",FACE,{"disambiguationData":[OSD([sQuery(id+"F2.wireOp",EDGE,"E22.MirrorCS")])]}),"instanceName":"1"})]})]});}
            var Q3;
            {var subQ0=sQuery(id+"F1.wireOp",EDGE,"E1");var subQ1=sQuery(id+"F1.wireOp",EDGE,"E0");var subQ3=sQuery(id+"F2.wireOp",EDGE,"E19");var subQ5=sQuery(id+"F2.wireOp",EDGE,"E15");Q3=makeQuery(id+"F7.boolean.opBoolean","SPLIT",EDGE,{"disambiguationData":[TD([makeQuery(id+"F3.opExtrude","CAP_FACE",FACE,{"disambiguationData":[OSD([subQ1,subQ0])],"isStart":true})])],"derivedFrom":makeQuery(id+"F4.opExtrude","SWEPT_EDGE",EDGE,{"disambiguationData":[OSD([subQ5,subQ3])]})});}
            var Q4;
            {var subQ0=sQuery(id+"F1.wireOp",EDGE,"E1");var subQ1=sQuery(id+"F1.wireOp",EDGE,"E0");var subQ2=sQuery(id+"F2.wireOp",EDGE,"E25.MirrorCS");var subQ3=sQuery(id+"F2.wireOp",EDGE,"E22.MirrorCS");Q4=makeQuery(id+"F7.boolean.opBoolean","SPLIT",EDGE,{"disambiguationData":[TD([makeQuery(id+"F3.opExtrude","CAP_FACE",FACE,{"disambiguationData":[OSD([subQ1,subQ0])],"isStart":true})])],"derivedFrom":makeQuery(id+"F7.opPattern","COPY",EDGE,{"derivedFrom":makeQuery(id+"F4.opExtrude","SWEPT_EDGE",EDGE,{"disambiguationData":[OSD([subQ3,subQ2])]}),"instanceName":"1"})});}
            var Q5;
            {var subQ0=sQuery(id+"F1.wireOp",EDGE,"E1");Q5=makeQuery(id+"F8.opChamfer","TWEAK_EDGE",EDGE,{"derivedFrom":[makeQuery(id+"F7.boolean.opBoolean","TWEAK_VERTEX",VERTEX,{"derivedFrom":[makeQuery(id+"F3.opExtrude","CAP_FACE",FACE,{"disambiguationData":[OSD([sQuery(id+"F1.wireOp",EDGE,"E0"),subQ0])],"isStart":false}),makeQuery(id+"F3.opExtrude","SWEPT_FACE",FACE,{"disambiguationData":[OSD([subQ0])]}),makeQuery(id+"F7.opPattern","COPY",FACE,{"derivedFrom":makeQuery(id+"F4.opExtrude","SWEPT_FACE",FACE,{"disambiguationData":[OSD([sQuery(id+"F2.wireOp",EDGE,"E13"),sQuery(id+"F2.wireOp",EDGE,"E19"),sQuery(id+"F2.wireOp",EDGE,"E25.MirrorCS")])]}),"instanceName":"1"}),makeQuery(id+"F7.opPattern","COPY",FACE,{"derivedFrom":makeQuery(id+"F4.opExtrude","SWEPT_FACE",FACE,{"disambiguationData":[OSD([sQuery(id+"F2.wireOp",EDGE,"E15")])]}),"instanceName":"1"})]})]});}
            var Q6;
            {var subQ0=makeQuery(id+"F4.opExtrude","SWEPT_FACE",FACE,{"disambiguationData":[OSD([sQuery(id+"F2.wireOp",EDGE,"E13"),sQuery(id+"F2.wireOp",EDGE,"E19"),sQuery(id+"F2.wireOp",EDGE,"E25.MirrorCS")])]});var subQ1=sQuery(id+"F1.wireOp",EDGE,"E1");Q6=makeQuery(id+"F7.boolean.opBoolean","SPLIT",EDGE,{"disambiguationData":[TD([makeQuery(id+"F3.opExtrude","CAP_FACE",FACE,{"disambiguationData":[OSD([sQuery(id+"F1.wireOp",EDGE,"E0"),subQ1])],"isStart":false}),makeQuery(id+"F3.opExtrude","SWEPT_FACE",FACE,{"disambiguationData":[OSD([subQ1])]}),makeQuery(id+"F7.opPattern","COPY",FACE,{"derivedFrom":subQ0,"instanceName":"1"}),makeQuery(id+"F7.opPattern","COPY",FACE,{"derivedFrom":makeQuery(id+"F4.opExtrude","SWEPT_FACE",FACE,{"disambiguationData":[OSD([sQuery(id+"F2.wireOp",EDGE,"E15")])]}),"instanceName":"1"}),makeQuery(id+"F7.opPattern","COPY",FACE,{"derivedFrom":subQ0,"instanceName":"2"}),makeQuery(id+"F7.opPattern","COPY",FACE,{"derivedFrom":makeQuery(id+"F4.opExtrude","SWEPT_FACE",FACE,{"disambiguationData":[OSD([sQuery(id+"F2.wireOp",EDGE,"E22.MirrorCS")])]}),"instanceName":"2"})])],"derivedFrom":makeQuery(id+"F3.opExtrude","CAP_EDGE",EDGE,{"disambiguationData":[OSD([subQ1])],"isStart":false})});}
            var Q7;
            {var subQ0=sQuery(id+"F1.wireOp",EDGE,"E1");Q7=makeQuery(id+"F8.opChamfer","TWEAK_EDGE",EDGE,{"derivedFrom":[makeQuery(id+"F7.boolean.opBoolean","TWEAK_VERTEX",VERTEX,{"derivedFrom":[makeQuery(id+"F3.opExtrude","CAP_FACE",FACE,{"disambiguationData":[OSD([sQuery(id+"F1.wireOp",EDGE,"E0"),subQ0])],"isStart":false}),makeQuery(id+"F3.opExtrude","SWEPT_FACE",FACE,{"disambiguationData":[OSD([subQ0])]}),makeQuery(id+"F7.opPattern","COPY",FACE,{"derivedFrom":makeQuery(id+"F4.opExtrude","SWEPT_FACE",FACE,{"disambiguationData":[OSD([sQuery(id+"F2.wireOp",EDGE,"E13"),sQuery(id+"F2.wireOp",EDGE,"E19"),sQuery(id+"F2.wireOp",EDGE,"E25.MirrorCS")])]}),"instanceName":"2"}),makeQuery(id+"F7.opPattern","COPY",FACE,{"derivedFrom":makeQuery(id+"F4.opExtrude","SWEPT_FACE",FACE,{"disambiguationData":[OSD([sQuery(id+"F2.wireOp",EDGE,"E22.MirrorCS")])]}),"instanceName":"2"})]})]});}
            var Q8;
            {var subQ0=sQuery(id+"F1.wireOp",EDGE,"E1");var subQ1=sQuery(id+"F1.wireOp",EDGE,"E0");var subQ2=sQuery(id+"F2.wireOp",EDGE,"E25.MirrorCS");var subQ3=sQuery(id+"F2.wireOp",EDGE,"E22.MirrorCS");Q8=makeQuery(id+"F7.boolean.opBoolean","SPLIT",EDGE,{"disambiguationData":[TD([makeQuery(id+"F3.opExtrude","CAP_FACE",FACE,{"disambiguationData":[OSD([subQ1,subQ0])],"isStart":true})])],"derivedFrom":makeQuery(id+"F7.opPattern","COPY",EDGE,{"derivedFrom":makeQuery(id+"F4.opExtrude","SWEPT_EDGE",EDGE,{"disambiguationData":[OSD([subQ3,subQ2])]}),"instanceName":"2"})});}
            var Q9;
            {var subQ0=sQuery(id+"F1.wireOp",EDGE,"E1");var subQ1=sQuery(id+"F1.wireOp",EDGE,"E0");var subQ3=sQuery(id+"F2.wireOp",EDGE,"E19");var subQ4=sQuery(id+"F2.wireOp",EDGE,"E15");Q9=makeQuery(id+"F7.boolean.opBoolean","SPLIT",EDGE,{"disambiguationData":[TD([makeQuery(id+"F3.opExtrude","CAP_FACE",FACE,{"disambiguationData":[OSD([subQ1,subQ0])],"isStart":true})])],"derivedFrom":makeQuery(id+"F7.opPattern","COPY",EDGE,{"derivedFrom":makeQuery(id+"F4.opExtrude","SWEPT_EDGE",EDGE,{"disambiguationData":[OSD([subQ4,subQ3])]}),"instanceName":"1"})});}
            var Q10;
            {var subQ0=sQuery(id+"F1.wireOp",EDGE,"E1");var subQ1=sQuery(id+"F2.wireOp",EDGE,"E22.MirrorCS");var subQ2=sQuery(id+"F1.wireOp",EDGE,"E0");var subQ3=sQuery(id+"F2.wireOp",EDGE,"E25.MirrorCS");Q10=makeQuery(id+"F7.boolean.opBoolean","SPLIT",EDGE,{"disambiguationData":[TD([makeQuery(id+"F3.opExtrude","CAP_FACE",FACE,{"disambiguationData":[OSD([subQ2,subQ0])],"isStart":true})])],"derivedFrom":makeQuery(id+"F4.opExtrude","SWEPT_EDGE",EDGE,{"disambiguationData":[OSD([subQ1,subQ3])]})});}
            var Q11;
            {var subQ0=sQuery(id+"F1.wireOp",EDGE,"E1");var subQ1=sQuery(id+"F1.wireOp",EDGE,"E0");var subQ2=sQuery(id+"F2.wireOp",EDGE,"E15");var subQ4=sQuery(id+"F2.wireOp",EDGE,"E19");Q11=makeQuery(id+"F7.boolean.opBoolean","SPLIT",EDGE,{"disambiguationData":[TD([makeQuery(id+"F3.opExtrude","CAP_FACE",FACE,{"disambiguationData":[OSD([subQ1,subQ0])],"isStart":true})])],"derivedFrom":makeQuery(id+"F7.opPattern","COPY",EDGE,{"derivedFrom":makeQuery(id+"F4.opExtrude","SWEPT_EDGE",EDGE,{"disambiguationData":[OSD([subQ2,subQ4])]}),"instanceName":"2"})});}
            var Q12;
            {var subQ0=sQuery(id+"F1.wireOp",EDGE,"E1");var subQ1=makeQuery(id+"F4.opExtrude","SWEPT_FACE",FACE,{"disambiguationData":[OSD([sQuery(id+"F2.wireOp",EDGE,"E13"),sQuery(id+"F2.wireOp",EDGE,"E19"),sQuery(id+"F2.wireOp",EDGE,"E25.MirrorCS")])]});Q12=makeQuery(id+"F7.boolean.opBoolean","SPLIT",EDGE,{"disambiguationData":[TD([makeQuery(id+"F3.opExtrude","CAP_FACE",FACE,{"disambiguationData":[OSD([sQuery(id+"F1.wireOp",EDGE,"E0"),subQ0])],"isStart":false}),makeQuery(id+"F3.opExtrude","SWEPT_FACE",FACE,{"disambiguationData":[OSD([subQ0])]}),subQ1,makeQuery(id+"F4.opExtrude","SWEPT_FACE",FACE,{"disambiguationData":[OSD([sQuery(id+"F2.wireOp",EDGE,"E22.MirrorCS")])]}),makeQuery(id+"F7.opPattern","COPY",FACE,{"derivedFrom":subQ1,"instanceName":"2"}),makeQuery(id+"F7.opPattern","COPY",FACE,{"derivedFrom":makeQuery(id+"F4.opExtrude","SWEPT_FACE",FACE,{"disambiguationData":[OSD([sQuery(id+"F2.wireOp",EDGE,"E15")])]}),"instanceName":"2"})])],"derivedFrom":makeQuery(id+"F3.opExtrude","CAP_EDGE",EDGE,{"disambiguationData":[OSD([subQ0])],"isStart":false})});}
            var Q13;
            {var subQ0=sQuery(id+"F1.wireOp",EDGE,"E1");Q13=makeQuery(id+"F8.opChamfer","TWEAK_EDGE",EDGE,{"derivedFrom":[makeQuery(id+"F7.boolean.opBoolean","TWEAK_VERTEX",VERTEX,{"derivedFrom":[makeQuery(id+"F3.opExtrude","CAP_FACE",FACE,{"disambiguationData":[OSD([sQuery(id+"F1.wireOp",EDGE,"E0"),subQ0])],"isStart":false}),makeQuery(id+"F3.opExtrude","SWEPT_FACE",FACE,{"disambiguationData":[OSD([subQ0])]}),makeQuery(id+"F4.opExtrude","SWEPT_FACE",FACE,{"disambiguationData":[OSD([sQuery(id+"F2.wireOp",EDGE,"E13"),sQuery(id+"F2.wireOp",EDGE,"E19"),sQuery(id+"F2.wireOp",EDGE,"E25.MirrorCS")])]}),makeQuery(id+"F4.opExtrude","SWEPT_FACE",FACE,{"disambiguationData":[OSD([sQuery(id+"F2.wireOp",EDGE,"E22.MirrorCS")])]})]})]});}
            var Q14;
            {var subQ0=sQuery(id+"F1.wireOp",EDGE,"E1");Q14=makeQuery(id+"F8.opChamfer","TWEAK_EDGE",EDGE,{"derivedFrom":[makeQuery(id+"F7.boolean.opBoolean","TWEAK_VERTEX",VERTEX,{"derivedFrom":[makeQuery(id+"F3.opExtrude","CAP_FACE",FACE,{"disambiguationData":[OSD([sQuery(id+"F1.wireOp",EDGE,"E0"),subQ0])],"isStart":false}),makeQuery(id+"F3.opExtrude","SWEPT_FACE",FACE,{"disambiguationData":[OSD([subQ0])]}),makeQuery(id+"F7.opPattern","COPY",FACE,{"derivedFrom":makeQuery(id+"F4.opExtrude","SWEPT_FACE",FACE,{"disambiguationData":[OSD([sQuery(id+"F2.wireOp",EDGE,"E13"),sQuery(id+"F2.wireOp",EDGE,"E19"),sQuery(id+"F2.wireOp",EDGE,"E25.MirrorCS")])]}),"instanceName":"2"}),makeQuery(id+"F7.opPattern","COPY",FACE,{"derivedFrom":makeQuery(id+"F4.opExtrude","SWEPT_FACE",FACE,{"disambiguationData":[OSD([sQuery(id+"F2.wireOp",EDGE,"E15")])]}),"instanceName":"2"})]})]});}
            fillet(context, id + "F11", {"entities" : qUnion([Q0, Q1, Q2, Q3, Q4, Q5, Q6, Q7, Q8, Q9, Q10, Q11, Q12, Q13, Q14]), "radius" : 2 * mm, "tangentPropagation" : true, "allowEdgeOverflow" : false});
        }
        {
            var Q0;
            Q0=makeQuery(id+"F7.opPattern","COPY",EDGE,{"derivedFrom":makeQuery(id+"F4.opExtrude","CAP_EDGE",EDGE,{"disambiguationData":[OSD([sQuery(id+"F2.wireOp",EDGE,"E21.MirrorCS")])],"isStart":true}),"instanceName":"2"});
            var Q1;
            Q1=makeQuery(id+"F7.opPattern","COPY",EDGE,{"derivedFrom":makeQuery(id+"F4.opExtrude","CAP_EDGE",EDGE,{"disambiguationData":[OSD([sQuery(id+"F2.wireOp",EDGE,"E10")])],"isStart":true}),"instanceName":"2"});
            var Q2;
            Q2=makeQuery(id+"F7.opPattern","COPY",EDGE,{"derivedFrom":makeQuery(id+"F4.opExtrude","CAP_EDGE",EDGE,{"disambiguationData":[OSD([sQuery(id+"F2.wireOp",EDGE,"E12")])],"isStart":true}),"instanceName":"2"});
            var Q3;
            Q3=makeQuery(id+"F7.opPattern","COPY",EDGE,{"derivedFrom":makeQuery(id+"F4.opExtrude","CAP_EDGE",EDGE,{"disambiguationData":[OSD([sQuery(id+"F2.wireOp",EDGE,"E12")])],"isStart":true}),"instanceName":"1"});
            var Q4;
            Q4=makeQuery(id+"F7.opPattern","COPY",EDGE,{"derivedFrom":makeQuery(id+"F4.opExtrude","CAP_EDGE",EDGE,{"disambiguationData":[OSD([sQuery(id+"F2.wireOp",EDGE,"E10")])],"isStart":true}),"instanceName":"1"});
            var Q5;
            Q5=makeQuery(id+"F7.opPattern","COPY",EDGE,{"derivedFrom":makeQuery(id+"F4.opExtrude","CAP_EDGE",EDGE,{"disambiguationData":[OSD([sQuery(id+"F2.wireOp",EDGE,"E21.MirrorCS")])],"isStart":true}),"instanceName":"1"});
            var Q6;
            Q6=makeQuery(id+"F4.opExtrude","CAP_EDGE",EDGE,{"disambiguationData":[OSD([sQuery(id+"F2.wireOp",EDGE,"E12")])],"isStart":true});
            var Q7;
            Q7=makeQuery(id+"F4.opExtrude","CAP_EDGE",EDGE,{"disambiguationData":[OSD([sQuery(id+"F2.wireOp",EDGE,"E10")])],"isStart":true});
            var Q8;
            Q8=makeQuery(id+"F4.opExtrude","CAP_EDGE",EDGE,{"disambiguationData":[OSD([sQuery(id+"F2.wireOp",EDGE,"E21.MirrorCS")])],"isStart":true});
            chamfer(context, id + "F12", {"entities" : qUnion([Q0, Q1, Q2, Q3, Q4, Q5, Q6, Q7, Q8]), "width" : 6 * mm, "tangentPropagation" : true});
        }
        {
            var Q0;
            {var subQ0=sQuery(id+"F2.wireOp",EDGE,"E10");Q0=makeQuery(id+"F12.opChamfer","BLEND_EDGE",EDGE,{"blendedFrom":[makeQuery(id+"F7.opPattern","COPY",EDGE,{"derivedFrom":makeQuery(id+"F4.opExtrude","CAP_EDGE",EDGE,{"disambiguationData":[OSD([subQ0])],"isStart":true}),"instanceName":"1"}),makeQuery(id+"F7.opPattern","COPY",FACE,{"derivedFrom":makeQuery(id+"F4.opExtrude","SWEPT_FACE",FACE,{"disambiguationData":[OSD([subQ0])]}),"instanceName":"1"})],"blendedInto":[makeQuery(id+"F7.opPattern","COPY",FACE,{"derivedFrom":makeQuery(id+"F4.opExtrude","SWEPT_FACE",FACE,{"disambiguationData":[OSD([subQ0])]}),"instanceName":"1"})]});}
            var Q1;
            {var subQ0=sQuery(id+"F2.wireOp",EDGE,"E12");Q1=makeQuery(id+"F12.opChamfer","BLEND_EDGE",EDGE,{"blendedFrom":[makeQuery(id+"F7.opPattern","COPY",EDGE,{"derivedFrom":makeQuery(id+"F4.opExtrude","CAP_EDGE",EDGE,{"disambiguationData":[OSD([subQ0])],"isStart":true}),"instanceName":"1"}),makeQuery(id+"F7.opPattern","COPY",FACE,{"derivedFrom":makeQuery(id+"F4.opExtrude","SWEPT_FACE",FACE,{"disambiguationData":[OSD([subQ0])]}),"instanceName":"1"})],"blendedInto":[makeQuery(id+"F7.opPattern","COPY",FACE,{"derivedFrom":makeQuery(id+"F4.opExtrude","SWEPT_FACE",FACE,{"disambiguationData":[OSD([subQ0])]}),"instanceName":"1"})]});}
            var Q2;
            {var subQ0=sQuery(id+"F2.wireOp",EDGE,"E21.MirrorCS");Q2=makeQuery(id+"F12.opChamfer","BLEND_EDGE",EDGE,{"blendedFrom":[makeQuery(id+"F7.opPattern","COPY",EDGE,{"derivedFrom":makeQuery(id+"F4.opExtrude","CAP_EDGE",EDGE,{"disambiguationData":[OSD([subQ0])],"isStart":true}),"instanceName":"1"}),makeQuery(id+"F7.opPattern","COPY",FACE,{"derivedFrom":makeQuery(id+"F4.opExtrude","SWEPT_FACE",FACE,{"disambiguationData":[OSD([subQ0])]}),"instanceName":"1"})],"blendedInto":[makeQuery(id+"F7.opPattern","COPY",FACE,{"derivedFrom":makeQuery(id+"F4.opExtrude","SWEPT_FACE",FACE,{"disambiguationData":[OSD([subQ0])]}),"instanceName":"1"})]});}
            var Q3;
            {var subQ0=sQuery(id+"F2.wireOp",EDGE,"E12");Q3=makeQuery(id+"F12.opChamfer","BLEND_EDGE",EDGE,{"blendedFrom":[makeQuery(id+"F4.opExtrude","CAP_EDGE",EDGE,{"disambiguationData":[OSD([subQ0])],"isStart":true}),makeQuery(id+"F4.opExtrude","SWEPT_FACE",FACE,{"disambiguationData":[OSD([subQ0])]})],"blendedInto":[makeQuery(id+"F4.opExtrude","SWEPT_FACE",FACE,{"disambiguationData":[OSD([subQ0])]})]});}
            var Q4;
            {var subQ0=sQuery(id+"F2.wireOp",EDGE,"E10");Q4=makeQuery(id+"F12.opChamfer","BLEND_EDGE",EDGE,{"blendedFrom":[makeQuery(id+"F4.opExtrude","CAP_EDGE",EDGE,{"disambiguationData":[OSD([subQ0])],"isStart":true}),makeQuery(id+"F4.opExtrude","SWEPT_FACE",FACE,{"disambiguationData":[OSD([subQ0])]})],"blendedInto":[makeQuery(id+"F4.opExtrude","SWEPT_FACE",FACE,{"disambiguationData":[OSD([subQ0])]})]});}
            var Q5;
            {var subQ0=sQuery(id+"F2.wireOp",EDGE,"E21.MirrorCS");Q5=makeQuery(id+"F12.opChamfer","BLEND_EDGE",EDGE,{"blendedFrom":[makeQuery(id+"F4.opExtrude","CAP_EDGE",EDGE,{"disambiguationData":[OSD([subQ0])],"isStart":true}),makeQuery(id+"F4.opExtrude","SWEPT_FACE",FACE,{"disambiguationData":[OSD([subQ0])]})],"blendedInto":[makeQuery(id+"F4.opExtrude","SWEPT_FACE",FACE,{"disambiguationData":[OSD([subQ0])]})]});}
            var Q6;
            {var subQ0=sQuery(id+"F2.wireOp",EDGE,"E12");Q6=makeQuery(id+"F12.opChamfer","BLEND_EDGE",EDGE,{"blendedFrom":[makeQuery(id+"F7.opPattern","COPY",EDGE,{"derivedFrom":makeQuery(id+"F4.opExtrude","CAP_EDGE",EDGE,{"disambiguationData":[OSD([subQ0])],"isStart":true}),"instanceName":"2"}),makeQuery(id+"F7.opPattern","COPY",FACE,{"derivedFrom":makeQuery(id+"F4.opExtrude","SWEPT_FACE",FACE,{"disambiguationData":[OSD([subQ0])]}),"instanceName":"2"})],"blendedInto":[makeQuery(id+"F7.opPattern","COPY",FACE,{"derivedFrom":makeQuery(id+"F4.opExtrude","SWEPT_FACE",FACE,{"disambiguationData":[OSD([subQ0])]}),"instanceName":"2"})]});}
            var Q7;
            {var subQ0=sQuery(id+"F2.wireOp",EDGE,"E10");Q7=makeQuery(id+"F12.opChamfer","BLEND_EDGE",EDGE,{"blendedFrom":[makeQuery(id+"F7.opPattern","COPY",EDGE,{"derivedFrom":makeQuery(id+"F4.opExtrude","CAP_EDGE",EDGE,{"disambiguationData":[OSD([subQ0])],"isStart":true}),"instanceName":"2"}),makeQuery(id+"F7.opPattern","COPY",FACE,{"derivedFrom":makeQuery(id+"F4.opExtrude","SWEPT_FACE",FACE,{"disambiguationData":[OSD([subQ0])]}),"instanceName":"2"})],"blendedInto":[makeQuery(id+"F7.opPattern","COPY",FACE,{"derivedFrom":makeQuery(id+"F4.opExtrude","SWEPT_FACE",FACE,{"disambiguationData":[OSD([subQ0])]}),"instanceName":"2"})]});}
            var Q8;
            {var subQ0=sQuery(id+"F2.wireOp",EDGE,"E21.MirrorCS");Q8=makeQuery(id+"F12.opChamfer","BLEND_EDGE",EDGE,{"blendedFrom":[makeQuery(id+"F7.opPattern","COPY",EDGE,{"derivedFrom":makeQuery(id+"F4.opExtrude","CAP_EDGE",EDGE,{"disambiguationData":[OSD([subQ0])],"isStart":true}),"instanceName":"2"}),makeQuery(id+"F7.opPattern","COPY",FACE,{"derivedFrom":makeQuery(id+"F4.opExtrude","SWEPT_FACE",FACE,{"disambiguationData":[OSD([subQ0])]}),"instanceName":"2"})],"blendedInto":[makeQuery(id+"F7.opPattern","COPY",FACE,{"derivedFrom":makeQuery(id+"F4.opExtrude","SWEPT_FACE",FACE,{"disambiguationData":[OSD([subQ0])]}),"instanceName":"2"})]});}
            fillet(context, id + "F13", {"entities" : qUnion([Q0, Q1, Q2, Q3, Q4, Q5, Q6, Q7, Q8]), "radius" : 5 * mm, "tangentPropagation" : true, "allowEdgeOverflow" : false});
        }
        {
            var Q0;
            Q0=makeQuery(id+"F4.opExtrude","SWEPT_FACE",FACE,{"disambiguationData":[OSD([sQuery(id+"F2.wireOp",EDGE,"E11")])]});
            cPlane(context, id + "F14", {"entities" : qUnion([Q0]), "cplaneType" : CPlaneType.OFFSET, "offset" : 4 * mm, "oppositeDirection" : true, "width" : 150 * mm, "height" : 150 * mm});
        }
        {
            var Q0;
            Q0=qCreatedBy(id+"F14.planeOp",FACE);
            var sketch = newSketch(context, id + "F15", { "sketchPlane" : qUnion([Q0])});
            skCircle(sketch, "E27", {"center": v(-41, 9.5) * mm, "radius": 3.1 * mm});
            skLineSegment(sketch, "E28", {"start": v(-37.9, 9.5) * mm, "end": v(-37.9, 15.05) * mm});
            skLineSegment(sketch, "E29", {"start": v(-37.9, 15.05) * mm, "end": v(-44.1, 15.05) * mm});
            skLineSegment(sketch, "E30", {"start": v(-44.1, 15.05) * mm, "end": v(-44.1, 9.5) * mm});
            skSolve(sketch);
        }
        {
            var Q0;
            Q0=qSketchRegion(id+"F15",true);
            extrude(context, id + "F16", {"entities" : qUnion([Q0]), "oppositeDirection" : true, "depth" : 4 * mm});
        }
        {
            var Q0;
            Q0=makeQuery(id+"F16.opExtrude","SWEPT_BODY",BODY,{"disambiguationData":[OSD([sQuery(id+"F15.wireOp",EDGE,"E27"),sQuery(id+"F15.wireOp",EDGE,"E28"),sQuery(id+"F15.wireOp",EDGE,"E29"),sQuery(id+"F15.wireOp",EDGE,"E30")])]});
            var Q1;
            Q1=qCreatedBy(makeId("Right.planeOp"),FACE);
            mirror(context, id + "F17", {"entities" : qUnion([Q0]), "mirrorPlane" : qUnion([Q1])});
        }
        {
            var Q0;
            Q0=makeQuery(id+"F17.opPattern","COPY",BODY,{"derivedFrom":makeQuery(id+"F16.opExtrude","SWEPT_BODY",BODY,{"disambiguationData":[OSD([sQuery(id+"F15.wireOp",EDGE,"E27"),sQuery(id+"F15.wireOp",EDGE,"E28"),sQuery(id+"F15.wireOp",EDGE,"E29"),sQuery(id+"F15.wireOp",EDGE,"E30")])]}),"instanceName":"1"});
            var Q1;
            Q1=makeQuery(id+"F16.opExtrude","SWEPT_BODY",BODY,{"disambiguationData":[OSD([sQuery(id+"F15.wireOp",EDGE,"E27"),sQuery(id+"F15.wireOp",EDGE,"E28"),sQuery(id+"F15.wireOp",EDGE,"E29"),sQuery(id+"F15.wireOp",EDGE,"E30")])]});
            var Q2;
            Q2=makeQuery(id+"F3.opExtrude","SWEPT_FACE",FACE,{"disambiguationData":[OSD([sQuery(id+"F1.wireOp",EDGE,"E0")])]});
            circularPattern(context, id + "F18", {"operationType" : NewBodyOperationType.REMOVE, "entities" : qUnion([Q0, Q1]), "axis" : qUnion([Q2]), "angle" : 120 * degree, "instanceCount" : round(3)});
        }
        {
            var Q0;
            {var subQ0=sQuery(id+"F2.wireOp",EDGE,"E10");Q0=makeQuery(id+"F18.boolean.opBoolean","INTERSECT",EDGE,{"derivedFrom":[makeQuery(id+"F10.opFillet","BLEND_FACE",FACE,{"disambiguationData":[OSD([subQ0]),TDD([makeQuery(id+"F4.opExtrude","CAP_EDGE",EDGE,{"disambiguationData":[OSD([subQ0])],"isStart":false})])]}),makeQuery(id+"F17.opPattern","COPY",FACE,{"derivedFrom":makeQuery(id+"F16.opExtrude","SWEPT_FACE",FACE,{"disambiguationData":[OSD([sQuery(id+"F15.wireOp",EDGE,"E30")])]}),"instanceName":"1"})]});}
            var Q1;
            {var subQ0=sQuery(id+"F2.wireOp",EDGE,"E25.MirrorCS");var subQ1=sQuery(id+"F2.wireOp",EDGE,"E19");var subQ2=sQuery(id+"F2.wireOp",EDGE,"E13");Q1=makeQuery(id+"F18.boolean.opBoolean","INTERSECT",EDGE,{"derivedFrom":[makeQuery(id+"F9.opFillet","SPLIT",FACE,{"disambiguationData":[OD(0.0)],"derivedFrom":makeQuery(id+"F8.opChamfer","BLEND_FACE",FACE,{"disambiguationData":[OSD([subQ2,subQ1,subQ0]),TDD([makeQuery(id+"F4.opExtrude","CAP_EDGE",EDGE,{"disambiguationData":[OSD([subQ2,subQ1,subQ0])],"isStart":false})])]})}),makeQuery(id+"F17.opPattern","COPY",FACE,{"derivedFrom":makeQuery(id+"F16.opExtrude","SWEPT_FACE",FACE,{"disambiguationData":[OSD([sQuery(id+"F15.wireOp",EDGE,"E28")])]}),"instanceName":"1"})]});}
            var Q2;
            {var subQ0=sQuery(id+"F2.wireOp",EDGE,"E25.MirrorCS");var subQ1=sQuery(id+"F2.wireOp",EDGE,"E19");var subQ2=sQuery(id+"F2.wireOp",EDGE,"E13");Q2=makeQuery(id+"F18.boolean.opBoolean","INTERSECT",EDGE,{"derivedFrom":[makeQuery(id+"F9.opFillet","SPLIT",FACE,{"disambiguationData":[OD(0.0)],"derivedFrom":makeQuery(id+"F8.opChamfer","BLEND_FACE",FACE,{"disambiguationData":[OSD([subQ2,subQ1,subQ0]),TDD([makeQuery(id+"F4.opExtrude","CAP_EDGE",EDGE,{"disambiguationData":[OSD([subQ2,subQ1,subQ0])],"isStart":false})])]})}),makeQuery(id+"F16.opExtrude","SWEPT_FACE",FACE,{"disambiguationData":[OSD([sQuery(id+"F15.wireOp",EDGE,"E28")])]})]});}
            var Q3;
            {var subQ0=sQuery(id+"F2.wireOp",EDGE,"E10");Q3=makeQuery(id+"F18.boolean.opBoolean","INTERSECT",EDGE,{"derivedFrom":[makeQuery(id+"F10.opFillet","BLEND_FACE",FACE,{"disambiguationData":[OSD([subQ0]),TDD([makeQuery(id+"F4.opExtrude","CAP_EDGE",EDGE,{"disambiguationData":[OSD([subQ0])],"isStart":false})])]}),makeQuery(id+"F16.opExtrude","SWEPT_FACE",FACE,{"disambiguationData":[OSD([sQuery(id+"F15.wireOp",EDGE,"E30")])]})]});}
            var Q4;
            Q4=makeQuery(id+"F18.boolean.opBoolean","INTERSECT",EDGE,{"derivedFrom":[makeQuery(id+"F8.opChamfer","SPLIT",FACE,{"disambiguationData":[OD(0.0)],"derivedFrom":makeQuery(id+"F4.opExtrude","CAP_FACE",FACE,{"disambiguationData":[OSD([sQuery(id+"F2.wireOp",EDGE,"E9"),sQuery(id+"F2.wireOp",EDGE,"E10"),sQuery(id+"F2.wireOp",EDGE,"E11"),sQuery(id+"F2.wireOp",EDGE,"E12"),sQuery(id+"F2.wireOp",EDGE,"E13"),sQuery(id+"F2.wireOp",EDGE,"E14"),sQuery(id+"F2.wireOp",EDGE,"E15"),sQuery(id+"F2.wireOp",EDGE,"E17"),sQuery(id+"F2.wireOp",EDGE,"E18"),sQuery(id+"F2.wireOp",EDGE,"E19"),sQuery(id+"F2.wireOp",EDGE,"E20.MirrorCS"),sQuery(id+"F2.wireOp",EDGE,"E21.MirrorCS"),sQuery(id+"F2.wireOp",EDGE,"E22.MirrorCS"),sQuery(id+"F2.wireOp",EDGE,"E23.MirrorCS"),sQuery(id+"F2.wireOp",EDGE,"E24.MirrorCS"),sQuery(id+"F2.wireOp",EDGE,"E25.MirrorCS")])],"isStart":false})}),makeQuery(id+"F16.opExtrude","CAP_FACE",FACE,{"disambiguationData":[OSD([sQuery(id+"F15.wireOp",EDGE,"E27"),sQuery(id+"F15.wireOp",EDGE,"E28"),sQuery(id+"F15.wireOp",EDGE,"E29"),sQuery(id+"F15.wireOp",EDGE,"E30")])],"isStart":false})]});
            var Q5;
            Q5=makeQuery(id+"F18.boolean.opBoolean","INTERSECT",EDGE,{"derivedFrom":[makeQuery(id+"F8.opChamfer","SPLIT",FACE,{"disambiguationData":[OD(0.0)],"derivedFrom":makeQuery(id+"F4.opExtrude","CAP_FACE",FACE,{"disambiguationData":[OSD([sQuery(id+"F2.wireOp",EDGE,"E9"),sQuery(id+"F2.wireOp",EDGE,"E10"),sQuery(id+"F2.wireOp",EDGE,"E11"),sQuery(id+"F2.wireOp",EDGE,"E12"),sQuery(id+"F2.wireOp",EDGE,"E13"),sQuery(id+"F2.wireOp",EDGE,"E14"),sQuery(id+"F2.wireOp",EDGE,"E15"),sQuery(id+"F2.wireOp",EDGE,"E17"),sQuery(id+"F2.wireOp",EDGE,"E18"),sQuery(id+"F2.wireOp",EDGE,"E19"),sQuery(id+"F2.wireOp",EDGE,"E20.MirrorCS"),sQuery(id+"F2.wireOp",EDGE,"E21.MirrorCS"),sQuery(id+"F2.wireOp",EDGE,"E22.MirrorCS"),sQuery(id+"F2.wireOp",EDGE,"E23.MirrorCS"),sQuery(id+"F2.wireOp",EDGE,"E24.MirrorCS"),sQuery(id+"F2.wireOp",EDGE,"E25.MirrorCS")])],"isStart":false})}),makeQuery(id+"F16.opExtrude","CAP_FACE",FACE,{"disambiguationData":[OSD([sQuery(id+"F15.wireOp",EDGE,"E27"),sQuery(id+"F15.wireOp",EDGE,"E28"),sQuery(id+"F15.wireOp",EDGE,"E29"),sQuery(id+"F15.wireOp",EDGE,"E30")])],"isStart":true})]});
            var Q6;
            Q6=makeQuery(id+"F18.boolean.opBoolean","INTERSECT",EDGE,{"derivedFrom":[makeQuery(id+"F8.opChamfer","SPLIT",FACE,{"disambiguationData":[OD(0.0)],"derivedFrom":makeQuery(id+"F4.opExtrude","CAP_FACE",FACE,{"disambiguationData":[OSD([sQuery(id+"F2.wireOp",EDGE,"E9"),sQuery(id+"F2.wireOp",EDGE,"E10"),sQuery(id+"F2.wireOp",EDGE,"E11"),sQuery(id+"F2.wireOp",EDGE,"E12"),sQuery(id+"F2.wireOp",EDGE,"E13"),sQuery(id+"F2.wireOp",EDGE,"E14"),sQuery(id+"F2.wireOp",EDGE,"E15"),sQuery(id+"F2.wireOp",EDGE,"E17"),sQuery(id+"F2.wireOp",EDGE,"E18"),sQuery(id+"F2.wireOp",EDGE,"E19"),sQuery(id+"F2.wireOp",EDGE,"E20.MirrorCS"),sQuery(id+"F2.wireOp",EDGE,"E21.MirrorCS"),sQuery(id+"F2.wireOp",EDGE,"E22.MirrorCS"),sQuery(id+"F2.wireOp",EDGE,"E23.MirrorCS"),sQuery(id+"F2.wireOp",EDGE,"E24.MirrorCS"),sQuery(id+"F2.wireOp",EDGE,"E25.MirrorCS")])],"isStart":false})}),makeQuery(id+"F17.opPattern","COPY",FACE,{"derivedFrom":makeQuery(id+"F16.opExtrude","CAP_FACE",FACE,{"disambiguationData":[OSD([sQuery(id+"F15.wireOp",EDGE,"E27"),sQuery(id+"F15.wireOp",EDGE,"E28"),sQuery(id+"F15.wireOp",EDGE,"E29"),sQuery(id+"F15.wireOp",EDGE,"E30")])],"isStart":false}),"instanceName":"1"})]});
            var Q7;
            Q7=makeQuery(id+"F18.boolean.opBoolean","INTERSECT",EDGE,{"derivedFrom":[makeQuery(id+"F8.opChamfer","SPLIT",FACE,{"disambiguationData":[OD(0.0)],"derivedFrom":makeQuery(id+"F4.opExtrude","CAP_FACE",FACE,{"disambiguationData":[OSD([sQuery(id+"F2.wireOp",EDGE,"E9"),sQuery(id+"F2.wireOp",EDGE,"E10"),sQuery(id+"F2.wireOp",EDGE,"E11"),sQuery(id+"F2.wireOp",EDGE,"E12"),sQuery(id+"F2.wireOp",EDGE,"E13"),sQuery(id+"F2.wireOp",EDGE,"E14"),sQuery(id+"F2.wireOp",EDGE,"E15"),sQuery(id+"F2.wireOp",EDGE,"E17"),sQuery(id+"F2.wireOp",EDGE,"E18"),sQuery(id+"F2.wireOp",EDGE,"E19"),sQuery(id+"F2.wireOp",EDGE,"E20.MirrorCS"),sQuery(id+"F2.wireOp",EDGE,"E21.MirrorCS"),sQuery(id+"F2.wireOp",EDGE,"E22.MirrorCS"),sQuery(id+"F2.wireOp",EDGE,"E23.MirrorCS"),sQuery(id+"F2.wireOp",EDGE,"E24.MirrorCS"),sQuery(id+"F2.wireOp",EDGE,"E25.MirrorCS")])],"isStart":false})}),makeQuery(id+"F17.opPattern","COPY",FACE,{"derivedFrom":makeQuery(id+"F16.opExtrude","CAP_FACE",FACE,{"disambiguationData":[OSD([sQuery(id+"F15.wireOp",EDGE,"E27"),sQuery(id+"F15.wireOp",EDGE,"E28"),sQuery(id+"F15.wireOp",EDGE,"E29"),sQuery(id+"F15.wireOp",EDGE,"E30")])],"isStart":true}),"instanceName":"1"})]});
            var Q8;
            {var subQ0=sQuery(id+"F2.wireOp",EDGE,"E10");Q8=makeQuery(id+"F18.boolean.opBoolean","INTERSECT",EDGE,{"derivedFrom":[makeQuery(id+"F10.opFillet","BLEND_FACE",FACE,{"disambiguationData":[OSD([subQ0]),TDD([makeQuery(id+"F7.opPattern","COPY",EDGE,{"derivedFrom":makeQuery(id+"F4.opExtrude","CAP_EDGE",EDGE,{"disambiguationData":[OSD([subQ0])],"isStart":false}),"instanceName":"2"})])]}),makeQuery(id+"F18.opPattern","COPY",FACE,{"derivedFrom":makeQuery(id+"F17.opPattern","COPY",FACE,{"derivedFrom":makeQuery(id+"F16.opExtrude","SWEPT_FACE",FACE,{"disambiguationData":[OSD([sQuery(id+"F15.wireOp",EDGE,"E30")])]}),"instanceName":"1"}),"instanceName":"1"})]});}
            var Q9;
            {var subQ0=sQuery(id+"F2.wireOp",EDGE,"E25.MirrorCS");var subQ1=sQuery(id+"F2.wireOp",EDGE,"E19");var subQ2=sQuery(id+"F2.wireOp",EDGE,"E13");Q9=makeQuery(id+"F18.boolean.opBoolean","INTERSECT",EDGE,{"derivedFrom":[makeQuery(id+"F9.opFillet","SPLIT",FACE,{"disambiguationData":[OD(0.0)],"derivedFrom":makeQuery(id+"F8.opChamfer","BLEND_FACE",FACE,{"disambiguationData":[OSD([subQ2,subQ1,subQ0]),TDD([makeQuery(id+"F7.opPattern","COPY",EDGE,{"derivedFrom":makeQuery(id+"F4.opExtrude","CAP_EDGE",EDGE,{"disambiguationData":[OSD([subQ2,subQ1,subQ0])],"isStart":false}),"instanceName":"2"})])]})}),makeQuery(id+"F18.opPattern","COPY",FACE,{"derivedFrom":makeQuery(id+"F17.opPattern","COPY",FACE,{"derivedFrom":makeQuery(id+"F16.opExtrude","SWEPT_FACE",FACE,{"disambiguationData":[OSD([sQuery(id+"F15.wireOp",EDGE,"E28")])]}),"instanceName":"1"}),"instanceName":"1"})]});}
            var Q10;
            Q10=makeQuery(id+"F18.boolean.opBoolean","INTERSECT",EDGE,{"derivedFrom":[makeQuery(id+"F8.opChamfer","SPLIT",FACE,{"disambiguationData":[OD(0.0)],"derivedFrom":makeQuery(id+"F7.opPattern","COPY",FACE,{"derivedFrom":makeQuery(id+"F4.opExtrude","CAP_FACE",FACE,{"disambiguationData":[OSD([sQuery(id+"F2.wireOp",EDGE,"E9"),sQuery(id+"F2.wireOp",EDGE,"E10"),sQuery(id+"F2.wireOp",EDGE,"E11"),sQuery(id+"F2.wireOp",EDGE,"E12"),sQuery(id+"F2.wireOp",EDGE,"E13"),sQuery(id+"F2.wireOp",EDGE,"E14"),sQuery(id+"F2.wireOp",EDGE,"E15"),sQuery(id+"F2.wireOp",EDGE,"E17"),sQuery(id+"F2.wireOp",EDGE,"E18"),sQuery(id+"F2.wireOp",EDGE,"E19"),sQuery(id+"F2.wireOp",EDGE,"E20.MirrorCS"),sQuery(id+"F2.wireOp",EDGE,"E21.MirrorCS"),sQuery(id+"F2.wireOp",EDGE,"E22.MirrorCS"),sQuery(id+"F2.wireOp",EDGE,"E23.MirrorCS"),sQuery(id+"F2.wireOp",EDGE,"E24.MirrorCS"),sQuery(id+"F2.wireOp",EDGE,"E25.MirrorCS")])],"isStart":false}),"instanceName":"2"})}),makeQuery(id+"F18.opPattern","COPY",FACE,{"derivedFrom":makeQuery(id+"F17.opPattern","COPY",FACE,{"derivedFrom":makeQuery(id+"F16.opExtrude","CAP_FACE",FACE,{"disambiguationData":[OSD([sQuery(id+"F15.wireOp",EDGE,"E27"),sQuery(id+"F15.wireOp",EDGE,"E28"),sQuery(id+"F15.wireOp",EDGE,"E29"),sQuery(id+"F15.wireOp",EDGE,"E30")])],"isStart":false}),"instanceName":"1"}),"instanceName":"1"})]});
            var Q11;
            Q11=makeQuery(id+"F18.boolean.opBoolean","INTERSECT",EDGE,{"derivedFrom":[makeQuery(id+"F8.opChamfer","SPLIT",FACE,{"disambiguationData":[OD(0.0)],"derivedFrom":makeQuery(id+"F7.opPattern","COPY",FACE,{"derivedFrom":makeQuery(id+"F4.opExtrude","CAP_FACE",FACE,{"disambiguationData":[OSD([sQuery(id+"F2.wireOp",EDGE,"E9"),sQuery(id+"F2.wireOp",EDGE,"E10"),sQuery(id+"F2.wireOp",EDGE,"E11"),sQuery(id+"F2.wireOp",EDGE,"E12"),sQuery(id+"F2.wireOp",EDGE,"E13"),sQuery(id+"F2.wireOp",EDGE,"E14"),sQuery(id+"F2.wireOp",EDGE,"E15"),sQuery(id+"F2.wireOp",EDGE,"E17"),sQuery(id+"F2.wireOp",EDGE,"E18"),sQuery(id+"F2.wireOp",EDGE,"E19"),sQuery(id+"F2.wireOp",EDGE,"E20.MirrorCS"),sQuery(id+"F2.wireOp",EDGE,"E21.MirrorCS"),sQuery(id+"F2.wireOp",EDGE,"E22.MirrorCS"),sQuery(id+"F2.wireOp",EDGE,"E23.MirrorCS"),sQuery(id+"F2.wireOp",EDGE,"E24.MirrorCS"),sQuery(id+"F2.wireOp",EDGE,"E25.MirrorCS")])],"isStart":false}),"instanceName":"2"})}),makeQuery(id+"F18.opPattern","COPY",FACE,{"derivedFrom":makeQuery(id+"F17.opPattern","COPY",FACE,{"derivedFrom":makeQuery(id+"F16.opExtrude","CAP_FACE",FACE,{"disambiguationData":[OSD([sQuery(id+"F15.wireOp",EDGE,"E27"),sQuery(id+"F15.wireOp",EDGE,"E28"),sQuery(id+"F15.wireOp",EDGE,"E29"),sQuery(id+"F15.wireOp",EDGE,"E30")])],"isStart":true}),"instanceName":"1"}),"instanceName":"1"})]});
            var Q12;
            Q12=makeQuery(id+"F18.boolean.opBoolean","INTERSECT",EDGE,{"derivedFrom":[makeQuery(id+"F8.opChamfer","SPLIT",FACE,{"disambiguationData":[OD(0.0)],"derivedFrom":makeQuery(id+"F7.opPattern","COPY",FACE,{"derivedFrom":makeQuery(id+"F4.opExtrude","CAP_FACE",FACE,{"disambiguationData":[OSD([sQuery(id+"F2.wireOp",EDGE,"E9"),sQuery(id+"F2.wireOp",EDGE,"E10"),sQuery(id+"F2.wireOp",EDGE,"E11"),sQuery(id+"F2.wireOp",EDGE,"E12"),sQuery(id+"F2.wireOp",EDGE,"E13"),sQuery(id+"F2.wireOp",EDGE,"E14"),sQuery(id+"F2.wireOp",EDGE,"E15"),sQuery(id+"F2.wireOp",EDGE,"E17"),sQuery(id+"F2.wireOp",EDGE,"E18"),sQuery(id+"F2.wireOp",EDGE,"E19"),sQuery(id+"F2.wireOp",EDGE,"E20.MirrorCS"),sQuery(id+"F2.wireOp",EDGE,"E21.MirrorCS"),sQuery(id+"F2.wireOp",EDGE,"E22.MirrorCS"),sQuery(id+"F2.wireOp",EDGE,"E23.MirrorCS"),sQuery(id+"F2.wireOp",EDGE,"E24.MirrorCS"),sQuery(id+"F2.wireOp",EDGE,"E25.MirrorCS")])],"isStart":false}),"instanceName":"2"})}),makeQuery(id+"F18.opPattern","COPY",FACE,{"derivedFrom":makeQuery(id+"F16.opExtrude","CAP_FACE",FACE,{"disambiguationData":[OSD([sQuery(id+"F15.wireOp",EDGE,"E27"),sQuery(id+"F15.wireOp",EDGE,"E28"),sQuery(id+"F15.wireOp",EDGE,"E29"),sQuery(id+"F15.wireOp",EDGE,"E30")])],"isStart":true}),"instanceName":"1"})]});
            var Q13;
            Q13=makeQuery(id+"F18.boolean.opBoolean","INTERSECT",EDGE,{"derivedFrom":[makeQuery(id+"F8.opChamfer","SPLIT",FACE,{"disambiguationData":[OD(0.0)],"derivedFrom":makeQuery(id+"F7.opPattern","COPY",FACE,{"derivedFrom":makeQuery(id+"F4.opExtrude","CAP_FACE",FACE,{"disambiguationData":[OSD([sQuery(id+"F2.wireOp",EDGE,"E9"),sQuery(id+"F2.wireOp",EDGE,"E10"),sQuery(id+"F2.wireOp",EDGE,"E11"),sQuery(id+"F2.wireOp",EDGE,"E12"),sQuery(id+"F2.wireOp",EDGE,"E13"),sQuery(id+"F2.wireOp",EDGE,"E14"),sQuery(id+"F2.wireOp",EDGE,"E15"),sQuery(id+"F2.wireOp",EDGE,"E17"),sQuery(id+"F2.wireOp",EDGE,"E18"),sQuery(id+"F2.wireOp",EDGE,"E19"),sQuery(id+"F2.wireOp",EDGE,"E20.MirrorCS"),sQuery(id+"F2.wireOp",EDGE,"E21.MirrorCS"),sQuery(id+"F2.wireOp",EDGE,"E22.MirrorCS"),sQuery(id+"F2.wireOp",EDGE,"E23.MirrorCS"),sQuery(id+"F2.wireOp",EDGE,"E24.MirrorCS"),sQuery(id+"F2.wireOp",EDGE,"E25.MirrorCS")])],"isStart":false}),"instanceName":"2"})}),makeQuery(id+"F18.opPattern","COPY",FACE,{"derivedFrom":makeQuery(id+"F16.opExtrude","CAP_FACE",FACE,{"disambiguationData":[OSD([sQuery(id+"F15.wireOp",EDGE,"E27"),sQuery(id+"F15.wireOp",EDGE,"E28"),sQuery(id+"F15.wireOp",EDGE,"E29"),sQuery(id+"F15.wireOp",EDGE,"E30")])],"isStart":false}),"instanceName":"1"})]});
            var Q14;
            {var subQ0=sQuery(id+"F2.wireOp",EDGE,"E10");Q14=makeQuery(id+"F18.boolean.opBoolean","INTERSECT",EDGE,{"derivedFrom":[makeQuery(id+"F10.opFillet","BLEND_FACE",FACE,{"disambiguationData":[OSD([subQ0]),TDD([makeQuery(id+"F7.opPattern","COPY",EDGE,{"derivedFrom":makeQuery(id+"F4.opExtrude","CAP_EDGE",EDGE,{"disambiguationData":[OSD([subQ0])],"isStart":false}),"instanceName":"2"})])]}),makeQuery(id+"F18.opPattern","COPY",FACE,{"derivedFrom":makeQuery(id+"F16.opExtrude","SWEPT_FACE",FACE,{"disambiguationData":[OSD([sQuery(id+"F15.wireOp",EDGE,"E30")])]}),"instanceName":"1"})]});}
            var Q15;
            {var subQ0=sQuery(id+"F2.wireOp",EDGE,"E25.MirrorCS");var subQ1=sQuery(id+"F2.wireOp",EDGE,"E19");var subQ2=sQuery(id+"F2.wireOp",EDGE,"E13");Q15=makeQuery(id+"F18.boolean.opBoolean","INTERSECT",EDGE,{"derivedFrom":[makeQuery(id+"F9.opFillet","SPLIT",FACE,{"disambiguationData":[OD(0.0)],"derivedFrom":makeQuery(id+"F8.opChamfer","BLEND_FACE",FACE,{"disambiguationData":[OSD([subQ2,subQ1,subQ0]),TDD([makeQuery(id+"F7.opPattern","COPY",EDGE,{"derivedFrom":makeQuery(id+"F4.opExtrude","CAP_EDGE",EDGE,{"disambiguationData":[OSD([subQ2,subQ1,subQ0])],"isStart":false}),"instanceName":"2"})])]})}),makeQuery(id+"F18.opPattern","COPY",FACE,{"derivedFrom":makeQuery(id+"F16.opExtrude","SWEPT_FACE",FACE,{"disambiguationData":[OSD([sQuery(id+"F15.wireOp",EDGE,"E28")])]}),"instanceName":"1"})]});}
            var Q16;
            {var subQ0=sQuery(id+"F2.wireOp",EDGE,"E10");Q16=makeQuery(id+"F18.boolean.opBoolean","INTERSECT",EDGE,{"derivedFrom":[makeQuery(id+"F10.opFillet","BLEND_FACE",FACE,{"disambiguationData":[OSD([subQ0]),TDD([makeQuery(id+"F7.opPattern","COPY",EDGE,{"derivedFrom":makeQuery(id+"F4.opExtrude","CAP_EDGE",EDGE,{"disambiguationData":[OSD([subQ0])],"isStart":false}),"instanceName":"1"})])]}),makeQuery(id+"F18.opPattern","COPY",FACE,{"derivedFrom":makeQuery(id+"F16.opExtrude","SWEPT_FACE",FACE,{"disambiguationData":[OSD([sQuery(id+"F15.wireOp",EDGE,"E30")])]}),"instanceName":"2"})]});}
            var Q17;
            {var subQ0=sQuery(id+"F2.wireOp",EDGE,"E25.MirrorCS");var subQ1=sQuery(id+"F2.wireOp",EDGE,"E19");var subQ2=sQuery(id+"F2.wireOp",EDGE,"E13");Q17=makeQuery(id+"F18.boolean.opBoolean","INTERSECT",EDGE,{"derivedFrom":[makeQuery(id+"F9.opFillet","SPLIT",FACE,{"disambiguationData":[OD(0.0)],"derivedFrom":makeQuery(id+"F8.opChamfer","BLEND_FACE",FACE,{"disambiguationData":[OSD([subQ2,subQ1,subQ0]),TDD([makeQuery(id+"F7.opPattern","COPY",EDGE,{"derivedFrom":makeQuery(id+"F4.opExtrude","CAP_EDGE",EDGE,{"disambiguationData":[OSD([subQ2,subQ1,subQ0])],"isStart":false}),"instanceName":"1"})])]})}),makeQuery(id+"F18.opPattern","COPY",FACE,{"derivedFrom":makeQuery(id+"F16.opExtrude","SWEPT_FACE",FACE,{"disambiguationData":[OSD([sQuery(id+"F15.wireOp",EDGE,"E28")])]}),"instanceName":"2"})]});}
            var Q18;
            Q18=makeQuery(id+"F18.boolean.opBoolean","INTERSECT",EDGE,{"derivedFrom":[makeQuery(id+"F8.opChamfer","SPLIT",FACE,{"disambiguationData":[OD(0.0)],"derivedFrom":makeQuery(id+"F7.opPattern","COPY",FACE,{"derivedFrom":makeQuery(id+"F4.opExtrude","CAP_FACE",FACE,{"disambiguationData":[OSD([sQuery(id+"F2.wireOp",EDGE,"E9"),sQuery(id+"F2.wireOp",EDGE,"E10"),sQuery(id+"F2.wireOp",EDGE,"E11"),sQuery(id+"F2.wireOp",EDGE,"E12"),sQuery(id+"F2.wireOp",EDGE,"E13"),sQuery(id+"F2.wireOp",EDGE,"E14"),sQuery(id+"F2.wireOp",EDGE,"E15"),sQuery(id+"F2.wireOp",EDGE,"E17"),sQuery(id+"F2.wireOp",EDGE,"E18"),sQuery(id+"F2.wireOp",EDGE,"E19"),sQuery(id+"F2.wireOp",EDGE,"E20.MirrorCS"),sQuery(id+"F2.wireOp",EDGE,"E21.MirrorCS"),sQuery(id+"F2.wireOp",EDGE,"E22.MirrorCS"),sQuery(id+"F2.wireOp",EDGE,"E23.MirrorCS"),sQuery(id+"F2.wireOp",EDGE,"E24.MirrorCS"),sQuery(id+"F2.wireOp",EDGE,"E25.MirrorCS")])],"isStart":false}),"instanceName":"1"})}),makeQuery(id+"F18.opPattern","COPY",FACE,{"derivedFrom":makeQuery(id+"F16.opExtrude","CAP_FACE",FACE,{"disambiguationData":[OSD([sQuery(id+"F15.wireOp",EDGE,"E27"),sQuery(id+"F15.wireOp",EDGE,"E28"),sQuery(id+"F15.wireOp",EDGE,"E29"),sQuery(id+"F15.wireOp",EDGE,"E30")])],"isStart":true}),"instanceName":"2"})]});
            var Q19;
            Q19=makeQuery(id+"F18.boolean.opBoolean","INTERSECT",EDGE,{"derivedFrom":[makeQuery(id+"F8.opChamfer","SPLIT",FACE,{"disambiguationData":[OD(0.0)],"derivedFrom":makeQuery(id+"F7.opPattern","COPY",FACE,{"derivedFrom":makeQuery(id+"F4.opExtrude","CAP_FACE",FACE,{"disambiguationData":[OSD([sQuery(id+"F2.wireOp",EDGE,"E9"),sQuery(id+"F2.wireOp",EDGE,"E10"),sQuery(id+"F2.wireOp",EDGE,"E11"),sQuery(id+"F2.wireOp",EDGE,"E12"),sQuery(id+"F2.wireOp",EDGE,"E13"),sQuery(id+"F2.wireOp",EDGE,"E14"),sQuery(id+"F2.wireOp",EDGE,"E15"),sQuery(id+"F2.wireOp",EDGE,"E17"),sQuery(id+"F2.wireOp",EDGE,"E18"),sQuery(id+"F2.wireOp",EDGE,"E19"),sQuery(id+"F2.wireOp",EDGE,"E20.MirrorCS"),sQuery(id+"F2.wireOp",EDGE,"E21.MirrorCS"),sQuery(id+"F2.wireOp",EDGE,"E22.MirrorCS"),sQuery(id+"F2.wireOp",EDGE,"E23.MirrorCS"),sQuery(id+"F2.wireOp",EDGE,"E24.MirrorCS"),sQuery(id+"F2.wireOp",EDGE,"E25.MirrorCS")])],"isStart":false}),"instanceName":"1"})}),makeQuery(id+"F18.opPattern","COPY",FACE,{"derivedFrom":makeQuery(id+"F16.opExtrude","CAP_FACE",FACE,{"disambiguationData":[OSD([sQuery(id+"F15.wireOp",EDGE,"E27"),sQuery(id+"F15.wireOp",EDGE,"E28"),sQuery(id+"F15.wireOp",EDGE,"E29"),sQuery(id+"F15.wireOp",EDGE,"E30")])],"isStart":false}),"instanceName":"2"})]});
            var Q20;
            Q20=makeQuery(id+"F18.boolean.opBoolean","INTERSECT",EDGE,{"derivedFrom":[makeQuery(id+"F8.opChamfer","SPLIT",FACE,{"disambiguationData":[OD(0.0)],"derivedFrom":makeQuery(id+"F7.opPattern","COPY",FACE,{"derivedFrom":makeQuery(id+"F4.opExtrude","CAP_FACE",FACE,{"disambiguationData":[OSD([sQuery(id+"F2.wireOp",EDGE,"E9"),sQuery(id+"F2.wireOp",EDGE,"E10"),sQuery(id+"F2.wireOp",EDGE,"E11"),sQuery(id+"F2.wireOp",EDGE,"E12"),sQuery(id+"F2.wireOp",EDGE,"E13"),sQuery(id+"F2.wireOp",EDGE,"E14"),sQuery(id+"F2.wireOp",EDGE,"E15"),sQuery(id+"F2.wireOp",EDGE,"E17"),sQuery(id+"F2.wireOp",EDGE,"E18"),sQuery(id+"F2.wireOp",EDGE,"E19"),sQuery(id+"F2.wireOp",EDGE,"E20.MirrorCS"),sQuery(id+"F2.wireOp",EDGE,"E21.MirrorCS"),sQuery(id+"F2.wireOp",EDGE,"E22.MirrorCS"),sQuery(id+"F2.wireOp",EDGE,"E23.MirrorCS"),sQuery(id+"F2.wireOp",EDGE,"E24.MirrorCS"),sQuery(id+"F2.wireOp",EDGE,"E25.MirrorCS")])],"isStart":false}),"instanceName":"1"})}),makeQuery(id+"F18.opPattern","COPY",FACE,{"derivedFrom":makeQuery(id+"F17.opPattern","COPY",FACE,{"derivedFrom":makeQuery(id+"F16.opExtrude","CAP_FACE",FACE,{"disambiguationData":[OSD([sQuery(id+"F15.wireOp",EDGE,"E27"),sQuery(id+"F15.wireOp",EDGE,"E28"),sQuery(id+"F15.wireOp",EDGE,"E29"),sQuery(id+"F15.wireOp",EDGE,"E30")])],"isStart":true}),"instanceName":"1"}),"instanceName":"2"})]});
            var Q21;
            Q21=makeQuery(id+"F18.boolean.opBoolean","INTERSECT",EDGE,{"derivedFrom":[makeQuery(id+"F8.opChamfer","SPLIT",FACE,{"disambiguationData":[OD(0.0)],"derivedFrom":makeQuery(id+"F7.opPattern","COPY",FACE,{"derivedFrom":makeQuery(id+"F4.opExtrude","CAP_FACE",FACE,{"disambiguationData":[OSD([sQuery(id+"F2.wireOp",EDGE,"E9"),sQuery(id+"F2.wireOp",EDGE,"E10"),sQuery(id+"F2.wireOp",EDGE,"E11"),sQuery(id+"F2.wireOp",EDGE,"E12"),sQuery(id+"F2.wireOp",EDGE,"E13"),sQuery(id+"F2.wireOp",EDGE,"E14"),sQuery(id+"F2.wireOp",EDGE,"E15"),sQuery(id+"F2.wireOp",EDGE,"E17"),sQuery(id+"F2.wireOp",EDGE,"E18"),sQuery(id+"F2.wireOp",EDGE,"E19"),sQuery(id+"F2.wireOp",EDGE,"E20.MirrorCS"),sQuery(id+"F2.wireOp",EDGE,"E21.MirrorCS"),sQuery(id+"F2.wireOp",EDGE,"E22.MirrorCS"),sQuery(id+"F2.wireOp",EDGE,"E23.MirrorCS"),sQuery(id+"F2.wireOp",EDGE,"E24.MirrorCS"),sQuery(id+"F2.wireOp",EDGE,"E25.MirrorCS")])],"isStart":false}),"instanceName":"1"})}),makeQuery(id+"F18.opPattern","COPY",FACE,{"derivedFrom":makeQuery(id+"F17.opPattern","COPY",FACE,{"derivedFrom":makeQuery(id+"F16.opExtrude","CAP_FACE",FACE,{"disambiguationData":[OSD([sQuery(id+"F15.wireOp",EDGE,"E27"),sQuery(id+"F15.wireOp",EDGE,"E28"),sQuery(id+"F15.wireOp",EDGE,"E29"),sQuery(id+"F15.wireOp",EDGE,"E30")])],"isStart":false}),"instanceName":"1"}),"instanceName":"2"})]});
            var Q22;
            {var subQ0=sQuery(id+"F2.wireOp",EDGE,"E10");Q22=makeQuery(id+"F18.boolean.opBoolean","INTERSECT",EDGE,{"derivedFrom":[makeQuery(id+"F10.opFillet","BLEND_FACE",FACE,{"disambiguationData":[OSD([subQ0]),TDD([makeQuery(id+"F7.opPattern","COPY",EDGE,{"derivedFrom":makeQuery(id+"F4.opExtrude","CAP_EDGE",EDGE,{"disambiguationData":[OSD([subQ0])],"isStart":false}),"instanceName":"1"})])]}),makeQuery(id+"F18.opPattern","COPY",FACE,{"derivedFrom":makeQuery(id+"F17.opPattern","COPY",FACE,{"derivedFrom":makeQuery(id+"F16.opExtrude","SWEPT_FACE",FACE,{"disambiguationData":[OSD([sQuery(id+"F15.wireOp",EDGE,"E30")])]}),"instanceName":"1"}),"instanceName":"2"})]});}
            var Q23;
            {var subQ0=sQuery(id+"F2.wireOp",EDGE,"E25.MirrorCS");var subQ1=sQuery(id+"F2.wireOp",EDGE,"E19");var subQ2=sQuery(id+"F2.wireOp",EDGE,"E13");Q23=makeQuery(id+"F18.boolean.opBoolean","INTERSECT",EDGE,{"derivedFrom":[makeQuery(id+"F9.opFillet","SPLIT",FACE,{"disambiguationData":[OD(0.0)],"derivedFrom":makeQuery(id+"F8.opChamfer","BLEND_FACE",FACE,{"disambiguationData":[OSD([subQ2,subQ1,subQ0]),TDD([makeQuery(id+"F7.opPattern","COPY",EDGE,{"derivedFrom":makeQuery(id+"F4.opExtrude","CAP_EDGE",EDGE,{"disambiguationData":[OSD([subQ2,subQ1,subQ0])],"isStart":false}),"instanceName":"1"})])]})}),makeQuery(id+"F18.opPattern","COPY",FACE,{"derivedFrom":makeQuery(id+"F17.opPattern","COPY",FACE,{"derivedFrom":makeQuery(id+"F16.opExtrude","SWEPT_FACE",FACE,{"disambiguationData":[OSD([sQuery(id+"F15.wireOp",EDGE,"E28")])]}),"instanceName":"1"}),"instanceName":"2"})]});}
            fillet(context, id + "F19", {"entities" : qUnion([Q0, Q1, Q2, Q3, Q4, Q5, Q6, Q7, Q8, Q9, Q10, Q11, Q12, Q13, Q14, Q15, Q16, Q17, Q18, Q19, Q20, Q21, Q22, Q23]), "radius" : 0.3 * mm, "tangentPropagation" : true, "allowEdgeOverflow" : false});
        }
    });
